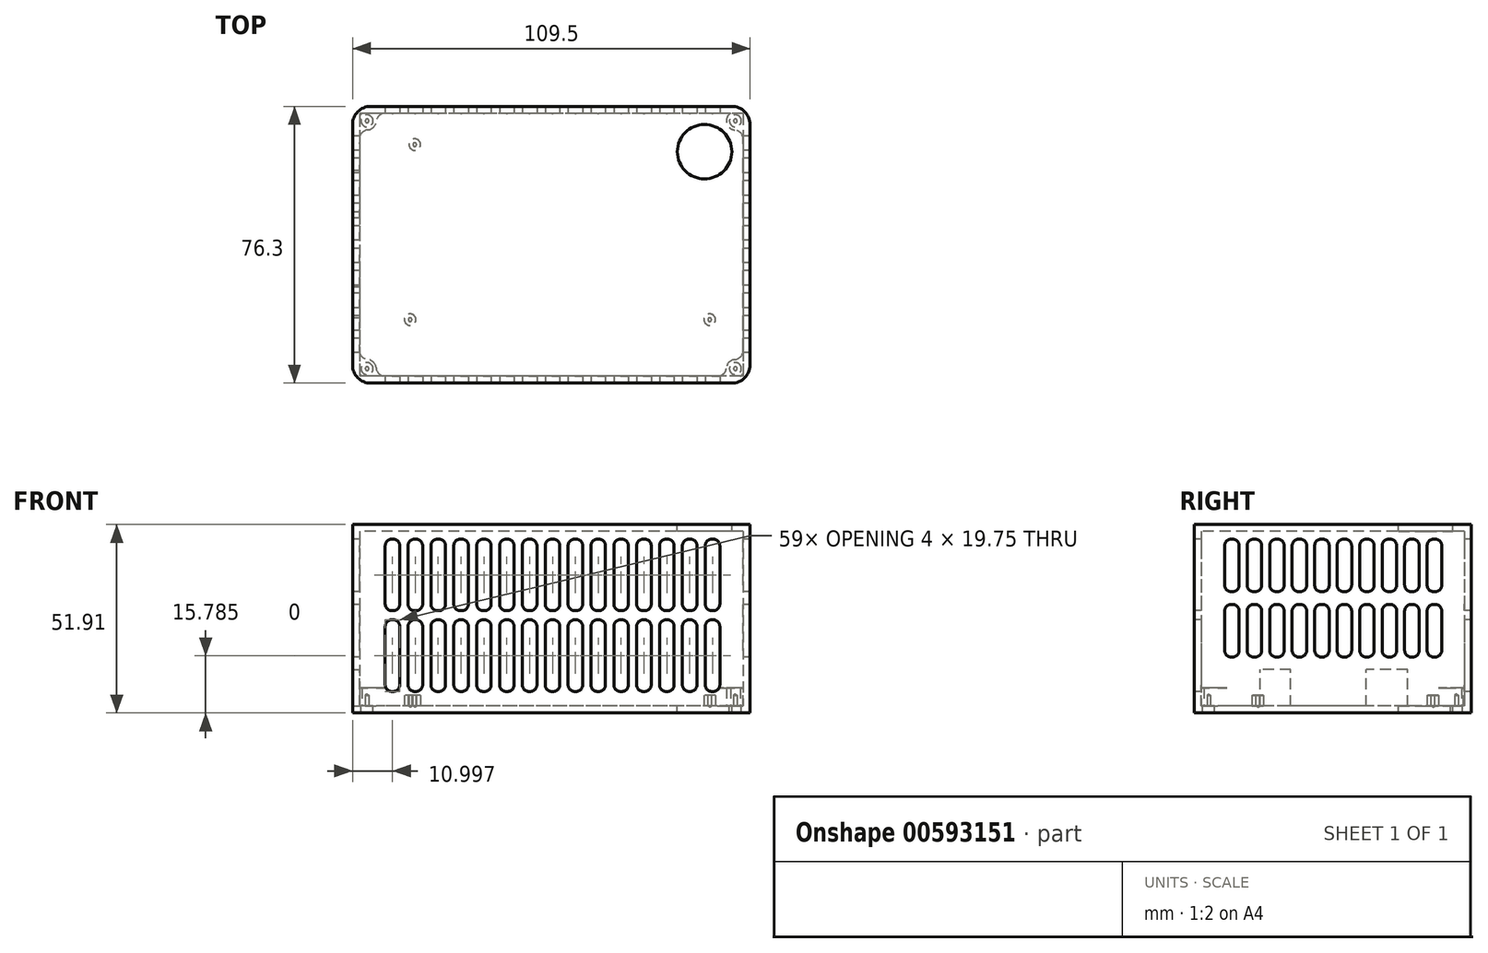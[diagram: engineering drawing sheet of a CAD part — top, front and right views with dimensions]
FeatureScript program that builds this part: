
annotation { "Feature Type Name" : "Feature", "Feature Type Description" : "" }
export const myFeature = defineFeature(function(context is Context, id is Id, definition is map)
    precondition{}
    {
        {
            var Q0;
            Q0=qCreatedBy(makeId("Top.planeOp"),FACE);
            var sketch = newSketch(context, id + "F0", { "sketchPlane" : qUnion([Q0])});
            skLineSegment(sketch, "E0.bottom", {"start": v(-36.54, 23.72) * mm, "end": v(59.98, 23.72) * mm});
            skLineSegment(sketch, "E0.top", {"start": v(-36.54, -29.62) * mm, "end": v(62.52, -29.62) * mm});
            skLineSegment(sketch, "E0.left", {"start": v(-36.54, 23.72) * mm, "end": v(-36.54, -29.62) * mm});
            skCircle(sketch, "E1", {"center": v(-21.3, 21.18) * mm, "radius": 1.59 * mm});
            skCircle(sketch, "E2", {"center": v(53.63, 21.18) * mm, "radius": 1.6 * mm});
            skCircle(sketch, "E3", {"center": v(-22.57, -27.08) * mm, "radius": 1.6 * mm});
            skCircle(sketch, "E4", {"center": v(59.98, -27.08) * mm, "radius": 1.6 * mm});
            skCircle(sketch, "E5", {"center": v(29.5, -22) * mm, "radius": 1.6 * mm});
            skCircle(sketch, "E6", {"center": v(29.5, 5.94) * mm, "radius": 1.6 * mm});
            skLineSegment(sketch, "E7.0", {"start": v(62.52, 21.18) * mm, "end": v(62.52, 11.02) * mm});
            skLineSegment(sketch, "E8.0", {"start": v(65.06, 8.48) * mm, "end": v(65.06, -25.81) * mm});
            skLineSegment(sketch, "E9", {"start": v(62.52, -28.35) * mm, "end": v(65.06, -25.81) * mm});
            skLineSegment(sketch, "E10", {"start": v(65.06, 8.48) * mm, "end": v(62.52, 11.02) * mm});
            skLineSegment(sketch, "E11", {"start": v(62.52, 21.18) * mm, "end": v(59.98, 23.72) * mm});
            skLineSegment(sketch, "E12", {"start": v(62.52, -28.35) * mm, "end": v(62.52, -29.62) * mm});
            skLineSegment(sketch, "E13.bottom", {"start": v(-42.89, 14.2) * mm, "end": v(-27.01, 14.2) * mm});
            skLineSegment(sketch, "E13.top", {"start": v(-42.89, 2.76) * mm, "end": v(-27.01, 2.76) * mm});
            skLineSegment(sketch, "E13.left", {"start": v(-42.89, 14.2) * mm, "end": v(-42.89, 2.76) * mm});
            skLineSegment(sketch, "E13.right", {"start": v(-27.01, 14.2) * mm, "end": v(-27.01, 2.76) * mm});
            skLineSegment(sketch, "E14.bottom", {"start": v(-38.44, -18.01) * mm, "end": v(-25.1, -18.01) * mm});
            skLineSegment(sketch, "E14.top", {"start": v(-38.44, -26.45) * mm, "end": v(-25.1, -26.45) * mm});
            skLineSegment(sketch, "E14.left", {"start": v(-38.44, -18.01) * mm, "end": v(-38.44, -26.45) * mm});
            skLineSegment(sketch, "E14.right", {"start": v(-25.1, -18.01) * mm, "end": v(-25.1, -26.45) * mm});
            skCircle(sketch, "E15", {"center": v(-17.74, 21.15) * mm, "radius": 0.51 * mm});
            skCircle(sketch, "E16.1.0.0", {"center": v(-15.2, 21.15) * mm, "radius": 0.51 * mm});
            skCircle(sketch, "E16.2.0.0", {"center": v(-12.66, 21.15) * mm, "radius": 0.51 * mm});
            skCircle(sketch, "E16.3.0.0", {"center": v(-10.12, 21.15) * mm, "radius": 0.51 * mm});
            skCircle(sketch, "E16.4.0.0", {"center": v(-7.58, 21.15) * mm, "radius": 0.51 * mm});
            skCircle(sketch, "E16.5.0.0", {"center": v(-5.04, 21.15) * mm, "radius": 0.51 * mm});
            skCircle(sketch, "E16.6.0.0", {"center": v(-2.5, 21.15) * mm, "radius": 0.51 * mm});
            skCircle(sketch, "E16.7.0.0", {"center": v(0.04, 21.15) * mm, "radius": 0.51 * mm});
            skCircle(sketch, "E16.8.0.0", {"center": v(2.58, 21.15) * mm, "radius": 0.51 * mm});
            skCircle(sketch, "E16.9.0.0", {"center": v(5.12, 21.15) * mm, "radius": 0.51 * mm});
            skLineSegment(sketch, "E16.direction1", {"start": v(-17.74, 21.15) * mm, "end": v(-15.2, 21.15) * mm, "construction": true});
            skCircle(sketch, "E17", {"center": v(9.18, 21.15) * mm, "radius": 0.5 * mm});
            skCircle(sketch, "E18.1.0.0", {"center": v(11.72, 21.15) * mm, "radius": 0.5 * mm});
            skCircle(sketch, "E18.2.0.0", {"center": v(14.26, 21.15) * mm, "radius": 0.5 * mm});
            skCircle(sketch, "E18.3.0.0", {"center": v(16.8, 21.15) * mm, "radius": 0.5 * mm});
            skCircle(sketch, "E18.4.0.0", {"center": v(19.34, 21.15) * mm, "radius": 0.5 * mm});
            skCircle(sketch, "E18.5.0.0", {"center": v(21.88, 21.15) * mm, "radius": 0.5 * mm});
            skCircle(sketch, "E18.6.0.0", {"center": v(24.42, 21.15) * mm, "radius": 0.5 * mm});
            skCircle(sketch, "E18.7.0.0", {"center": v(26.96, 21.15) * mm, "radius": 0.5 * mm});
            skLineSegment(sketch, "E18.direction1", {"start": v(9.18, 21.15) * mm, "end": v(11.72, 21.15) * mm, "construction": true});
            skCircle(sketch, "E19", {"center": v(32.04, 21.15) * mm, "radius": 0.5 * mm});
            skCircle(sketch, "E20.1.0.0", {"center": v(34.58, 21.15) * mm, "radius": 0.5 * mm});
            skCircle(sketch, "E20.2.0.0", {"center": v(37.12, 21.15) * mm, "radius": 0.5 * mm});
            skCircle(sketch, "E20.3.0.0", {"center": v(39.66, 21.15) * mm, "radius": 0.5 * mm});
            skCircle(sketch, "E20.4.0.0", {"center": v(42.2, 21.15) * mm, "radius": 0.5 * mm});
            skCircle(sketch, "E20.5.0.0", {"center": v(44.74, 21.15) * mm, "radius": 0.5 * mm});
            skCircle(sketch, "E20.6.0.0", {"center": v(47.28, 21.15) * mm, "radius": 0.5 * mm});
            skCircle(sketch, "E20.7.0.0", {"center": v(49.82, 21.15) * mm, "radius": 0.5 * mm});
            skLineSegment(sketch, "E20.direction1", {"start": v(32.04, 21.15) * mm, "end": v(34.58, 21.15) * mm, "construction": true});
            skCircle(sketch, "E21", {"center": v(-8.6, -27.08) * mm, "radius": 0.5 * mm});
            skCircle(sketch, "E22.1.0.0", {"center": v(-6.06, -27.08) * mm, "radius": 0.5 * mm});
            skCircle(sketch, "E22.2.0.0", {"center": v(-3.52, -27.08) * mm, "radius": 0.5 * mm});
            skCircle(sketch, "E22.3.0.0", {"center": v(-0.98, -27.08) * mm, "radius": 0.5 * mm});
            skCircle(sketch, "E22.4.0.0", {"center": v(1.56, -27.08) * mm, "radius": 0.5 * mm});
            skCircle(sketch, "E22.5.0.0", {"center": v(4.1, -27.08) * mm, "radius": 0.5 * mm});
            skCircle(sketch, "E22.6.0.0", {"center": v(6.64, -27.08) * mm, "radius": 0.5 * mm});
            skCircle(sketch, "E22.7.0.0", {"center": v(9.18, -27.08) * mm, "radius": 0.5 * mm});
            skLineSegment(sketch, "E22.direction1", {"start": v(-8.6, -27.08) * mm, "end": v(-6.06, -27.08) * mm, "construction": true});
            skCircle(sketch, "E23", {"center": v(14.66, -27.08) * mm, "radius": 0.51 * mm});
            skCircle(sketch, "E24.1.0.0", {"center": v(17.2, -27.08) * mm, "radius": 0.51 * mm});
            skCircle(sketch, "E24.2.0.0", {"center": v(19.74, -27.08) * mm, "radius": 0.51 * mm});
            skCircle(sketch, "E24.3.0.0", {"center": v(22.28, -27.08) * mm, "radius": 0.51 * mm});
            skCircle(sketch, "E24.4.0.0", {"center": v(24.82, -27.08) * mm, "radius": 0.51 * mm});
            skCircle(sketch, "E24.5.0.0", {"center": v(27.36, -27.08) * mm, "radius": 0.51 * mm});
            skCircle(sketch, "E24.6.0.0", {"center": v(29.9, -27.08) * mm, "radius": 0.51 * mm});
            skCircle(sketch, "E24.7.0.0", {"center": v(32.44, -27.08) * mm, "radius": 0.51 * mm});
            skLineSegment(sketch, "E24.direction1", {"start": v(14.66, -27.08) * mm, "end": v(17.2, -27.08) * mm, "construction": true});
            skCircle(sketch, "E25", {"center": v(37.12, -27.08) * mm, "radius": 0.5 * mm});
            skCircle(sketch, "E26.1.0.0", {"center": v(39.66, -27.08) * mm, "radius": 0.5 * mm});
            skCircle(sketch, "E26.2.0.0", {"center": v(42.2, -27.08) * mm, "radius": 0.5 * mm});
            skCircle(sketch, "E26.3.0.0", {"center": v(44.74, -27.08) * mm, "radius": 0.5 * mm});
            skCircle(sketch, "E26.4.0.0", {"center": v(47.28, -27.08) * mm, "radius": 0.5 * mm});
            skCircle(sketch, "E26.5.0.0", {"center": v(49.82, -27.08) * mm, "radius": 0.5 * mm});
            skCircle(sketch, "E26.6.0.0", {"center": v(52.36, -27.08) * mm, "radius": 0.5 * mm});
            skCircle(sketch, "E26.7.0.0", {"center": v(54.9, -27.08) * mm, "radius": 0.5 * mm});
            skLineSegment(sketch, "E26.direction1", {"start": v(37.12, -27.08) * mm, "end": v(39.66, -27.08) * mm, "construction": true});
            skCircle(sketch, "E27", {"center": v(59.98, 21.18) * mm, "radius": 0.5 * mm});
            skCircle(sketch, "E28.1.0.0", {"center": v(60, 18.64) * mm, "radius": 0.5 * mm});
            skCircle(sketch, "E28.2.0.0", {"center": v(60, 16.1) * mm, "radius": 0.5 * mm});
            skCircle(sketch, "E28.3.0.0", {"center": v(60, 13.56) * mm, "radius": 0.5 * mm});
            skCircle(sketch, "E28.4.0.0", {"center": v(60.02, 11.02) * mm, "radius": 0.5 * mm});
            skCircle(sketch, "E28.5.0.0", {"center": v(60.03, 8.48) * mm, "radius": 0.5 * mm});
            skCircle(sketch, "E28.6.0.0", {"center": v(60.04, 5.94) * mm, "radius": 0.5 * mm});
            skCircle(sketch, "E28.7.0.0", {"center": v(60.04, 3.4) * mm, "radius": 0.5 * mm});
            skCircle(sketch, "E28.8.0.0", {"center": v(60.05, 0.86) * mm, "radius": 0.5 * mm});
            skCircle(sketch, "E28.9.0.0", {"center": v(60.06, -1.68) * mm, "radius": 0.5 * mm});
            skCircle(sketch, "E28.10.0.0", {"center": v(60.07, -4.22) * mm, "radius": 0.5 * mm});
            skCircle(sketch, "E28.11.0.0", {"center": v(60.08, -6.76) * mm, "radius": 0.5 * mm});
            skCircle(sketch, "E28.12.0.0", {"center": v(60.09, -9.3) * mm, "radius": 0.5 * mm});
            skCircle(sketch, "E28.13.0.0", {"center": v(60.1, -11.84) * mm, "radius": 0.5 * mm});
            skCircle(sketch, "E28.14.0.0", {"center": v(60.1, -14.38) * mm, "radius": 0.5 * mm});
            skCircle(sketch, "E28.15.0.0", {"center": v(60.12, -16.92) * mm, "radius": 0.5 * mm});
            skCircle(sketch, "E28.16.0.0", {"center": v(60.13, -19.46) * mm, "radius": 0.5 * mm});
            skCircle(sketch, "E28.17.0.0", {"center": v(60.14, -22) * mm, "radius": 0.5 * mm});
            skLineSegment(sketch, "E28.direction1", {"start": v(59.98, 21.18) * mm, "end": v(60, 18.64) * mm, "construction": true});
            skCircle(sketch, "E29", {"center": v(57.44, 21.15) * mm, "radius": 0.5 * mm});
            skCircle(sketch, "E30.1.0.0", {"center": v(57.44, 18.61) * mm, "radius": 0.5 * mm});
            skCircle(sketch, "E30.2.0.0", {"center": v(57.43, 16.07) * mm, "radius": 0.5 * mm});
            skCircle(sketch, "E30.3.0.0", {"center": v(57.42, 13.53) * mm, "radius": 0.5 * mm});
            skCircle(sketch, "E30.4.0.0", {"center": v(57.42, 11) * mm, "radius": 0.5 * mm});
            skCircle(sketch, "E30.5.0.0", {"center": v(57.4, 8.45) * mm, "radius": 0.5 * mm});
            skCircle(sketch, "E30.6.0.0", {"center": v(57.4, 5.91) * mm, "radius": 0.5 * mm});
            skCircle(sketch, "E30.7.0.0", {"center": v(57.4, 3.37) * mm, "radius": 0.5 * mm});
            skCircle(sketch, "E30.8.0.0", {"center": v(57.39, 0.83) * mm, "radius": 0.5 * mm});
            skCircle(sketch, "E30.9.0.0", {"center": v(57.38, -1.7) * mm, "radius": 0.5 * mm});
            skCircle(sketch, "E30.10.0.0", {"center": v(57.38, -4.25) * mm, "radius": 0.5 * mm});
            skCircle(sketch, "E30.11.0.0", {"center": v(57.37, -6.79) * mm, "radius": 0.5 * mm});
            skCircle(sketch, "E30.12.0.0", {"center": v(57.36, -9.33) * mm, "radius": 0.5 * mm});
            skCircle(sketch, "E30.13.0.0", {"center": v(57.36, -11.87) * mm, "radius": 0.5 * mm});
            skCircle(sketch, "E30.14.0.0", {"center": v(57.35, -14.4) * mm, "radius": 0.5 * mm});
            skCircle(sketch, "E30.15.0.0", {"center": v(57.34, -16.95) * mm, "radius": 0.5 * mm});
            skCircle(sketch, "E30.16.0.0", {"center": v(57.34, -19.49) * mm, "radius": 0.5 * mm});
            skCircle(sketch, "E30.17.0.0", {"center": v(57.33, -22.03) * mm, "radius": 0.5 * mm});
            skLineSegment(sketch, "E30.direction1", {"start": v(57.44, 21.15) * mm, "end": v(57.44, 18.61) * mm, "construction": true});
            skCircle(sketch, "E31", {"center": v(27.09, 0.86) * mm, "radius": 0.5 * mm});
            skCircle(sketch, "E32", {"center": v(29.63, 0.86) * mm, "radius": 0.5 * mm});
            skCircle(sketch, "E33.1.0.0", {"center": v(27.1, -1.68) * mm, "radius": 0.5 * mm});
            skCircle(sketch, "E33.2.0.0", {"center": v(27.1, -4.22) * mm, "radius": 0.5 * mm});
            skLineSegment(sketch, "E33.direction1", {"start": v(27.09, 0.86) * mm, "end": v(27.1, -1.68) * mm, "construction": true});
            skCircle(sketch, "E34.1.0.0", {"center": v(29.62, -1.68) * mm, "radius": 0.5 * mm});
            skCircle(sketch, "E34.2.0.0", {"center": v(29.62, -4.22) * mm, "radius": 0.5 * mm});
            skLineSegment(sketch, "E34.direction1", {"start": v(29.63, 0.86) * mm, "end": v(29.62, -1.68) * mm, "construction": true});
            skSolve(sketch);
        }
        {
            var Q0;
            Q0=qCreatedBy(makeId("Top.planeOp"),FACE);
            var sketch = newSketch(context, id + "F1", { "sketchPlane" : qUnion([Q0])});
            skLineSegment(sketch, "E35.bottom", {"start": v(-36.54, 23.72) * mm, "end": v(65.06, 23.72) * mm});
            skLineSegment(sketch, "E35.top", {"start": v(-36.54, -36.58) * mm, "end": v(65.06, -36.58) * mm});
            skLineSegment(sketch, "E35.left", {"start": v(-36.54, 23.72) * mm, "end": v(-36.54, -36.58) * mm});
            skLineSegment(sketch, "E35.right", {"start": v(65.06, 23.72) * mm, "end": v(65.06, -36.58) * mm});
            skCircle(sketch, "E36", {"center": v(-21.3, 21.18) * mm, "radius": 1.9 * mm});
            skCircle(sketch, "E37", {"center": v(-22.54, -27.08) * mm, "radius": 1.9 * mm});
            skCircle(sketch, "E38", {"center": v(59.96, -27.08) * mm, "radius": 1.9 * mm});
            skLineSegment(sketch, "E39.0", {"start": v(-36.54, 23.72) * mm, "end": v(59.98, 23.72) * mm});
            skLineSegment(sketch, "E40.0", {"start": v(65.06, 8.48) * mm, "end": v(65.06, -25.81) * mm});
            skLineSegment(sketch, "E41.bottom", {"start": v(-39.16, -12.96) * mm, "end": v(-27.16, -12.96) * mm});
            skLineSegment(sketch, "E41.top", {"start": v(-39.16, -35.2) * mm, "end": v(-27.16, -35.2) * mm});
            skLineSegment(sketch, "E41.left", {"start": v(-39.16, -12.96) * mm, "end": v(-39.16, -35.2) * mm});
            skLineSegment(sketch, "E41.right", {"start": v(-27.16, -12.96) * mm, "end": v(-27.16, -35.2) * mm});
            skSolve(sketch);
        }
        {
            var Q0;
            Q0=qCreatedBy(makeId("Top.planeOp"),FACE);
            var sketch = newSketch(context, id + "F2", { "sketchPlane" : qUnion([Q0])});
            skLineSegment(sketch, "E42.bottom", {"start": v(71.06, 31.72) * mm, "end": v(-38.44, 31.72) * mm});
            skLineSegment(sketch, "E42.top", {"start": v(71.06, -44.58) * mm, "end": v(-38.44, -44.58) * mm});
            skLineSegment(sketch, "E42.left", {"start": v(71.06, 31.72) * mm, "end": v(71.06, -44.58) * mm});
            skLineSegment(sketch, "E43.0", {"start": v(-42.89, 14.2) * mm, "end": v(-42.89, 2.76) * mm});
            skLineSegment(sketch, "E44.0", {"start": v(-38.44, 31.72) * mm, "end": v(-38.44, -44.58) * mm});
            skSolve(sketch);
        }
        {
            var Q0;
            {var subQ1=sQuery(id+"F2.wireOp",EDGE,"E42.bottom");Q0=makeQuery(id+"F2.imprint","IMPRINT",FACE,{"disambiguationData":[TD([[makeQuery(id+"F2.imprint","IMPRINT",EDGE,{"derivedFrom":subQ1}),1.0]])]});}
            extrude(context, id + "F3", {"entities" : qUnion([Q0]), "depth" : 50 * mm, "offsetDistance" : 25 * mm});
        }
        {
            var Q0;
            Q0=makeQuery(id+"F3.opExtrude","CAP_FACE",FACE,{"disambiguationData":[OSD([sQuery(id+"F2.wireOp",EDGE,"E42.bottom"),sQuery(id+"F2.wireOp",EDGE,"E42.top"),sQuery(id+"F2.wireOp",EDGE,"E42.left"),sQuery(id+"F2.wireOp",EDGE,"E42.right"),sQuery(id+"F2.wireOp",EDGE,"E43.0")])],"isStart":true});
            shell(context, id + "F4", {"entities" : qUnion([Q0]), "thickness" : 1.9 * mm});
        }
        {
            var Q0;
            Q0=makeQuery(id+"F2.imprint","IMPRINT",FACE,{"disambiguationData":[TD([[makeQuery(id+"F2.imprint","IMPRINT",EDGE,{"derivedFrom":sQuery(id+"F2.wireOp",EDGE,"E42.bottom")}),1.0]])]});
            extrude(context, id + "F5", {"entities" : qUnion([Q0]), "oppositeDirection" : true, "depth" : 1.9 * mm, "offsetDistance" : 25 * mm});
        }
        {
            var Q0;
            {var subQ5=sQuery(id+"F0.wireOp",EDGE,"E13.right");Q0=makeQuery(id+"F0.imprint","IMPRINT",FACE,{"disambiguationData":[TD([[makeQuery(id+"F0.imprint","IMPRINT",EDGE,{"derivedFrom":subQ5}),-1.0]])]});}
            var Q1;
            {var subQ5=sQuery(id+"F0.wireOp",EDGE,"E13.left");Q1=makeQuery(id+"F0.imprint","IMPRINT",FACE,{"disambiguationData":[TD([[makeQuery(id+"F0.imprint","IMPRINT",EDGE,{"derivedFrom":subQ5}),1.0]])]});}
            extrude(context, id + "F6", {"entities" : qUnion([Q0, Q1]), "operationType" : NewBodyOperationType.REMOVE, "depth" : 10 * mm, "offsetDistance" : 25 * mm});
        }
        {
            var Q0;
            {var subQ5=sQuery(id+"F0.wireOp",EDGE,"E14.right");Q0=makeQuery(id+"F0.imprint","IMPRINT",FACE,{"disambiguationData":[TD([[makeQuery(id+"F0.imprint","IMPRINT",EDGE,{"derivedFrom":subQ5}),-1.0]])]});}
            var Q1;
            {var subQ5=sQuery(id+"F0.wireOp",EDGE,"E14.left");Q1=makeQuery(id+"F0.imprint","IMPRINT",FACE,{"disambiguationData":[TD([[makeQuery(id+"F0.imprint","IMPRINT",EDGE,{"derivedFrom":subQ5}),1.0]])]});}
            extrude(context, id + "F7", {"entities" : qUnion([Q0, Q1]), "operationType" : NewBodyOperationType.REMOVE, "depth" : 10 * mm, "offsetDistance" : 25 * mm});
        }
        {
            var Q0;
            Q0=makeQuery(id+"F0.imprint","IMPRINT",FACE,{"disambiguationData":[TD([[makeQuery(id+"F0.imprint","IMPRINT",EDGE,{"derivedFrom":sQuery(id+"F0.wireOp",EDGE,"E1")}),1.0]])]});
            var Q1;
            Q1=makeQuery(id+"F0.imprint","IMPRINT",FACE,{"disambiguationData":[TD([[makeQuery(id+"F0.imprint","IMPRINT",EDGE,{"derivedFrom":sQuery(id+"F0.wireOp",EDGE,"E3")}),1.0]])]});
            var Q2;
            Q2=makeQuery(id+"F0.imprint","IMPRINT",FACE,{"disambiguationData":[TD([[makeQuery(id+"F0.imprint","IMPRINT",EDGE,{"derivedFrom":sQuery(id+"F0.wireOp",EDGE,"E2")}),1.0]])]});
            var Q3;
            Q3=makeQuery(id+"F0.imprint","IMPRINT",FACE,{"disambiguationData":[TD([[makeQuery(id+"F0.imprint","IMPRINT",EDGE,{"derivedFrom":sQuery(id+"F0.wireOp",EDGE,"E4")}),1.0]])]});
            extrude(context, id + "F8", {"entities" : qUnion([Q0, Q1, Q2, Q3]), "operationType" : NewBodyOperationType.ADD, "depth" : 3 * mm, "offsetDistance" : 25 * mm});
        }
        {
            var Q0;
            Q0=makeQuery(id+"F2.imprint","IMPRINT",FACE,{"disambiguationData":[TD([[makeQuery(id+"F2.imprint","IMPRINT",EDGE,{"derivedFrom":sQuery(id+"F2.wireOp",EDGE,"E42.bottom")}),1.0]])]});
            var sketch = newSketch(context, id + "F9", { "sketchPlane" : qUnion([Q0])});
            skLineSegment(sketch, "E45.0", {"start": v(67.06, 27.72) * mm, "end": v(-34.44, 27.72) * mm});
            skLineSegment(sketch, "E45.1", {"start": v(67.06, 27.72) * mm, "end": v(67.06, -40.58) * mm});
            skLineSegment(sketch, "E45.2", {"start": v(67.06, -40.58) * mm, "end": v(-34.44, -40.58) * mm});
            skLineSegment(sketch, "E45.3", {"start": v(-34.44, 27.72) * mm, "end": v(-34.44, -40.58) * mm});
            skCircle(sketch, "E46", {"center": v(67.06, 27.72) * mm, "radius": 2.5 * mm});
            skCircle(sketch, "E47", {"center": v(67.06, -40.58) * mm, "radius": 2.5 * mm});
            skCircle(sketch, "E48", {"center": v(-34.44, 27.72) * mm, "radius": 2.5 * mm});
            skCircle(sketch, "E49", {"center": v(-34.44, -40.58) * mm, "radius": 2.5 * mm});
            skSolve(sketch);
        }
        {
            var Q0;
            Q0=sQuery(id+"F9.wireOp",VERTEX,"E45.0.end");
            var Q1;
            Q1=sQuery(id+"F9.wireOp",VERTEX,"E45.1.start");
            var Q2;
            Q2=sQuery(id+"F9.wireOp",VERTEX,"E45.1.end");
            var Q3;
            Q3=sQuery(id+"F9.wireOp",VERTEX,"E45.3.end");
            var Q4;
            Q4=makeQuery(id+"F5.opExtrude","SWEPT_BODY",BODY,{"disambiguationData":[OSD([sQuery(id+"F2.wireOp",EDGE,"E42.bottom"),sQuery(id+"F2.wireOp",EDGE,"E42.top"),sQuery(id+"F2.wireOp",EDGE,"E42.left"),sQuery(id+"F2.wireOp",EDGE,"E44.0")])]});
            hole(context, id + "F10", {"style" : HoleStyle.SIMPLE, "endStyle" : HoleEndStyle.THROUGH, "standardTappedOrClearance" : lookupTablePath({ "standard" : "ISO", "fit" : "Normal", "size" : "M3", "type" : "Clearance" }), "standardBlindInLast" : lookupTablePath({ "fit" : "Standard", "standard" : "ISO", "size" : "M3", "type" : "Clearance" }), "holeDiameter" : 3.3 * mm, "majorDiameter" : 5 * mm, "isTappedThrough" : true, "tappedDepth" : 12 * mm, "tapClearance" : 3, "locations" : qUnion([Q0, Q1, Q2, Q3]), "scope" : qUnion([Q4])});
        }
        {
            var Q0;
            Q0=makeQuery(id+"F8.opExtrude","CAP_FACE",FACE,{"disambiguationData":[OSD([sQuery(id+"F0.wireOp",EDGE,"E1")])],"isStart":false});
            var sketch = newSketch(context, id + "F11", { "sketchPlane" : qUnion([Q0])});
            skCircle(sketch, "E50.0", {"center": v(-22.57, -27.08) * mm, "radius": 1.6 * mm});
            skCircle(sketch, "E51.0", {"center": v(-21.3, 21.18) * mm, "radius": 1.59 * mm});
            skCircle(sketch, "E52.0", {"center": v(59.98, -27.08) * mm, "radius": 1.6 * mm});
            skCircle(sketch, "E53.0", {"center": v(53.63, 21.18) * mm, "radius": 1.6 * mm});
            skSolve(sketch);
        }
        {
            var Q0;
            Q0=sQuery(id+"F11.wireOp",VERTEX,"E50.0.center");
            var Q1;
            Q1=sQuery(id+"F11.wireOp",VERTEX,"E51.0.center");
            var Q2;
            Q2=sQuery(id+"F11.wireOp",VERTEX,"E52.0.center");
            var Q3;
            Q3=sQuery(id+"F11.wireOp",VERTEX,"E53.0.center");
            var Q4;
            Q4=makeQuery(id+"F5.opExtrude","SWEPT_BODY",BODY,{"disambiguationData":[OSD([sQuery(id+"F2.wireOp",EDGE,"E42.bottom"),sQuery(id+"F2.wireOp",EDGE,"E42.top"),sQuery(id+"F2.wireOp",EDGE,"E42.left"),sQuery(id+"F2.wireOp",EDGE,"E44.0")])]});
            hole(context, id + "F12", {"style" : HoleStyle.SIMPLE, "endStyle" : HoleEndStyle.BLIND, "standardTappedOrClearance" : lookupTablePath({ "standard" : "ISO", "size" : "1", "type" : "Drilled" }), "standardBlindInLast" : lookupTablePath({ "standard" : "ISO", "size" : "1", "type" : "Drilled" }), "holeDiameter" : 1 * mm, "majorDiameter" : 5 * mm, "holeDepth" : 3 * mm, "isTappedThrough" : true, "tappedDepth" : 12 * mm, "tapClearance" : 3, "locations" : qUnion([Q0, Q1, Q2, Q3]), "scope" : qUnion([Q4])});
        }
        {
            var Q0;
            {var subQ0=sQuery(id+"F9.wireOp",EDGE,"E45.1");var subQ1=sQuery(id+"F9.wireOp",EDGE,"E45.0");var subQ2=makeQuery(id+"F9.imprint","INTERSECT",VERTEX,{"derivedFrom":[subQ1,subQ0]});Q0=makeQuery(id+"F9.imprint","IMPRINT",FACE,{"disambiguationData":[TD([[makeQuery(id+"F9.imprint","IMPRINT",EDGE,{"disambiguationData":[TD([[subQ2,-1.0]])],"derivedFrom":subQ1}),-1.0]])]});}
            var Q1;
            {var subQ0=sQuery(id+"F9.wireOp",EDGE,"E45.1");var subQ1=sQuery(id+"F9.wireOp",EDGE,"E45.0");var subQ2=makeQuery(id+"F9.imprint","INTERSECT",VERTEX,{"derivedFrom":[subQ1,subQ0]});Q1=makeQuery(id+"F9.imprint","IMPRINT",FACE,{"disambiguationData":[TD([[makeQuery(id+"F9.imprint","IMPRINT",EDGE,{"disambiguationData":[TD([[subQ2,-1.0]])],"derivedFrom":subQ1}),1.0]])]});}
            var Q2;
            {var subQ0=sQuery(id+"F9.wireOp",EDGE,"E45.2");var subQ1=sQuery(id+"F9.wireOp",EDGE,"E45.1");var subQ2=makeQuery(id+"F9.imprint","INTERSECT",VERTEX,{"derivedFrom":[subQ1,subQ0]});Q2=makeQuery(id+"F9.imprint","IMPRINT",FACE,{"disambiguationData":[TD([[makeQuery(id+"F9.imprint","IMPRINT",EDGE,{"disambiguationData":[TD([[subQ2,1.0]])],"derivedFrom":subQ1}),-1.0]])]});}
            var Q3;
            {var subQ0=sQuery(id+"F9.wireOp",EDGE,"E45.2");var subQ1=sQuery(id+"F9.wireOp",EDGE,"E45.1");var subQ2=makeQuery(id+"F9.imprint","INTERSECT",VERTEX,{"derivedFrom":[subQ1,subQ0]});Q3=makeQuery(id+"F9.imprint","IMPRINT",FACE,{"disambiguationData":[TD([[makeQuery(id+"F9.imprint","IMPRINT",EDGE,{"disambiguationData":[TD([[subQ2,1.0]])],"derivedFrom":subQ1}),1.0]])]});}
            var Q4;
            {var subQ0=sQuery(id+"F9.wireOp",EDGE,"E45.3");var subQ1=sQuery(id+"F9.wireOp",EDGE,"E45.0");var subQ2=makeQuery(id+"F9.imprint","INTERSECT",VERTEX,{"derivedFrom":[subQ1,subQ0]});Q4=makeQuery(id+"F9.imprint","IMPRINT",FACE,{"disambiguationData":[TD([[makeQuery(id+"F9.imprint","IMPRINT",EDGE,{"disambiguationData":[TD([[subQ2,1.0]])],"derivedFrom":subQ1}),-1.0]])]});}
            var Q5;
            {var subQ0=sQuery(id+"F9.wireOp",EDGE,"E45.3");var subQ1=sQuery(id+"F9.wireOp",EDGE,"E45.0");var subQ2=makeQuery(id+"F9.imprint","INTERSECT",VERTEX,{"derivedFrom":[subQ1,subQ0]});Q5=makeQuery(id+"F9.imprint","IMPRINT",FACE,{"disambiguationData":[TD([[makeQuery(id+"F9.imprint","IMPRINT",EDGE,{"disambiguationData":[TD([[subQ2,1.0]])],"derivedFrom":subQ1}),1.0]])]});}
            var Q6;
            {var subQ0=sQuery(id+"F9.wireOp",EDGE,"E45.3");var subQ1=sQuery(id+"F9.wireOp",EDGE,"E45.2");var subQ2=makeQuery(id+"F9.imprint","INTERSECT",VERTEX,{"derivedFrom":[subQ1,subQ0]});Q6=makeQuery(id+"F9.imprint","IMPRINT",FACE,{"disambiguationData":[TD([[makeQuery(id+"F9.imprint","IMPRINT",EDGE,{"disambiguationData":[TD([[subQ2,1.0]])],"derivedFrom":subQ1}),-1.0]])]});}
            var Q7;
            {var subQ0=sQuery(id+"F9.wireOp",EDGE,"E45.3");var subQ1=sQuery(id+"F9.wireOp",EDGE,"E45.2");var subQ2=makeQuery(id+"F9.imprint","INTERSECT",VERTEX,{"derivedFrom":[subQ1,subQ0]});Q7=makeQuery(id+"F9.imprint","IMPRINT",FACE,{"disambiguationData":[TD([[makeQuery(id+"F9.imprint","IMPRINT",EDGE,{"disambiguationData":[TD([[subQ2,1.0]])],"derivedFrom":subQ1}),1.0]])]});}
            extrude(context, id + "F13", {"entities" : qUnion([Q0, Q1, Q2, Q3, Q4, Q5, Q6, Q7]), "operationType" : NewBodyOperationType.ADD, "depth" : 5 * mm, "offsetDistance" : 25 * mm});
        }
        {
            var Q0;
            Q0=sQuery(id+"F9.wireOp",VERTEX,"E49.center");
            var Q1;
            Q1=sQuery(id+"F9.wireOp",VERTEX,"E45.1.end");
            var Q2;
            Q2=sQuery(id+"F9.wireOp",VERTEX,"E45.0.end");
            var Q3;
            Q3=sQuery(id+"F9.wireOp",VERTEX,"E45.1.start");
            var Q4;
            Q4=makeQuery(id+"F3.opExtrude","SWEPT_BODY",BODY,{"disambiguationData":[OSD([sQuery(id+"F2.wireOp",EDGE,"E42.bottom"),sQuery(id+"F2.wireOp",EDGE,"E42.top"),sQuery(id+"F2.wireOp",EDGE,"E42.left"),sQuery(id+"F2.wireOp",EDGE,"E44.0")])]});
            hole(context, id + "F14", {"style" : HoleStyle.SIMPLE, "endStyle" : HoleEndStyle.BLIND, "oppositeDirection" : true, "standardTappedOrClearance" : lookupTablePath({ "standard" : "ISO", "size" : "1", "type" : "Drilled" }), "standardBlindInLast" : lookupTablePath({ "standard" : "ISO", "size" : "1", "type" : "Drilled" }), "holeDiameter" : 1 * mm, "majorDiameter" : 5 * mm, "holeDepth" : 3 * mm, "isTappedThrough" : true, "tappedDepth" : 12 * mm, "tapClearance" : 3, "locations" : qUnion([Q0, Q1, Q2, Q3]), "scope" : qUnion([Q4])});
        }
        {
            var Q0;
            Q0=makeQuery(id+"F13.boolean.opBoolean","INTERSECT",EDGE,{"disambiguationData":[OD(1.0)],"derivedFrom":[makeQuery(id+"F4.opShell","OFFSET_FACE",FACE,{"disambiguationData":[OSD([sQuery(id+"F2.wireOp",EDGE,"E42.left")])]}),makeQuery(id+"F13.opExtrude","SWEPT_FACE",FACE,{"disambiguationData":[OSD([sQuery(id+"F9.wireOp",EDGE,"E47")])]})]});
            var Q1;
            Q1=makeQuery(id+"F13.boolean.opBoolean","INTERSECT",EDGE,{"disambiguationData":[OD(1.0)],"derivedFrom":[makeQuery(id+"F4.opShell","OFFSET_FACE",FACE,{"disambiguationData":[OSD([sQuery(id+"F2.wireOp",EDGE,"E42.top")])]}),makeQuery(id+"F13.opExtrude","SWEPT_FACE",FACE,{"disambiguationData":[OSD([sQuery(id+"F9.wireOp",EDGE,"E47")])]})]});
            var Q2;
            Q2=makeQuery(id+"F13.boolean.opBoolean","INTERSECT",EDGE,{"disambiguationData":[OD(1.0)],"derivedFrom":[makeQuery(id+"F4.opShell","OFFSET_FACE",FACE,{"disambiguationData":[OSD([sQuery(id+"F2.wireOp",EDGE,"E42.left")])]}),makeQuery(id+"F13.opExtrude","SWEPT_FACE",FACE,{"disambiguationData":[OSD([sQuery(id+"F9.wireOp",EDGE,"E46")])]})]});
            var Q3;
            Q3=makeQuery(id+"F13.boolean.opBoolean","INTERSECT",EDGE,{"disambiguationData":[OD(1.0)],"derivedFrom":[makeQuery(id+"F4.opShell","OFFSET_FACE",FACE,{"disambiguationData":[OSD([sQuery(id+"F2.wireOp",EDGE,"E42.bottom")])]}),makeQuery(id+"F13.opExtrude","SWEPT_FACE",FACE,{"disambiguationData":[OSD([sQuery(id+"F9.wireOp",EDGE,"E46")])]})]});
            var Q4;
            Q4=makeQuery(id+"F13.boolean.opBoolean","INTERSECT",EDGE,{"disambiguationData":[OD(1.0)],"derivedFrom":[makeQuery(id+"F4.opShell","OFFSET_FACE",FACE,{"disambiguationData":[OSD([sQuery(id+"F2.wireOp",EDGE,"E42.top")])]}),makeQuery(id+"F13.opExtrude","SWEPT_FACE",FACE,{"disambiguationData":[OSD([sQuery(id+"F9.wireOp",EDGE,"E49")])]})]});
            var Q5;
            Q5=makeQuery(id+"F13.boolean.opBoolean","INTERSECT",EDGE,{"disambiguationData":[OD(1.0)],"derivedFrom":[makeQuery(id+"F4.opShell","OFFSET_FACE",FACE,{"disambiguationData":[OSD([sQuery(id+"F2.wireOp",EDGE,"E44.0")])]}),makeQuery(id+"F13.opExtrude","SWEPT_FACE",FACE,{"disambiguationData":[OSD([sQuery(id+"F9.wireOp",EDGE,"E49")])]})]});
            var Q6;
            Q6=makeQuery(id+"F13.boolean.opBoolean","INTERSECT",EDGE,{"disambiguationData":[OD(1.0)],"derivedFrom":[makeQuery(id+"F4.opShell","OFFSET_FACE",FACE,{"disambiguationData":[OSD([sQuery(id+"F2.wireOp",EDGE,"E44.0")])]}),makeQuery(id+"F13.opExtrude","SWEPT_FACE",FACE,{"disambiguationData":[OSD([sQuery(id+"F9.wireOp",EDGE,"E48")])]})]});
            var Q7;
            Q7=makeQuery(id+"F13.boolean.opBoolean","INTERSECT",EDGE,{"disambiguationData":[OD(1.0)],"derivedFrom":[makeQuery(id+"F4.opShell","OFFSET_FACE",FACE,{"disambiguationData":[OSD([sQuery(id+"F2.wireOp",EDGE,"E42.bottom")])]}),makeQuery(id+"F13.opExtrude","SWEPT_FACE",FACE,{"disambiguationData":[OSD([sQuery(id+"F9.wireOp",EDGE,"E48")])]})]});
            fillet(context, id + "F15", {"entities" : qUnion([Q0, Q1, Q2, Q3, Q4, Q5, Q6, Q7]), "radius" : 2.5 * mm, "tangentPropagation" : true, "allowEdgeOverflow" : false});
        }
        {
            var Q0;
            Q0=makeQuery(id+"F3.opExtrude","SWEPT_EDGE",EDGE,{"disambiguationData":[OSD([sQuery(id+"F2.wireOp",EDGE,"E42.top"),sQuery(id+"F2.wireOp",EDGE,"E44.0")])]});
            var Q1;
            Q1=makeQuery(id+"F3.opExtrude","SWEPT_EDGE",EDGE,{"disambiguationData":[OSD([sQuery(id+"F2.wireOp",EDGE,"E42.top"),sQuery(id+"F2.wireOp",EDGE,"E42.left")])]});
            var Q2;
            Q2=makeQuery(id+"F3.opExtrude","SWEPT_EDGE",EDGE,{"disambiguationData":[OSD([sQuery(id+"F2.wireOp",EDGE,"E42.bottom"),sQuery(id+"F2.wireOp",EDGE,"E44.0")])]});
            var Q3;
            Q3=makeQuery(id+"F3.opExtrude","SWEPT_EDGE",EDGE,{"disambiguationData":[OSD([sQuery(id+"F2.wireOp",EDGE,"E42.bottom"),sQuery(id+"F2.wireOp",EDGE,"E42.left")])]});
            var Q4;
            Q4=makeQuery(id+"F5.opExtrude","SWEPT_EDGE",EDGE,{"disambiguationData":[OSD([sQuery(id+"F2.wireOp",EDGE,"E42.bottom"),sQuery(id+"F2.wireOp",EDGE,"E44.0")])]});
            var Q5;
            Q5=makeQuery(id+"F5.opExtrude","SWEPT_EDGE",EDGE,{"disambiguationData":[OSD([sQuery(id+"F2.wireOp",EDGE,"E42.top"),sQuery(id+"F2.wireOp",EDGE,"E44.0")])]});
            var Q6;
            Q6=makeQuery(id+"F5.opExtrude","SWEPT_EDGE",EDGE,{"disambiguationData":[OSD([sQuery(id+"F2.wireOp",EDGE,"E42.top"),sQuery(id+"F2.wireOp",EDGE,"E42.left")])]});
            var Q7;
            Q7=makeQuery(id+"F5.opExtrude","SWEPT_EDGE",EDGE,{"disambiguationData":[OSD([sQuery(id+"F2.wireOp",EDGE,"E42.bottom"),sQuery(id+"F2.wireOp",EDGE,"E42.left")])]});
            fillet(context, id + "F16", {"entities" : qUnion([Q0, Q1, Q2, Q3, Q4, Q5, Q6, Q7]), "radius" : 5 * mm, "tangentPropagation" : true, "allowEdgeOverflow" : false});
        }
        {
            var Q0;
            Q0=makeQuery(id+"F3.opExtrude","SWEPT_FACE",FACE,{"disambiguationData":[OSD([sQuery(id+"F2.wireOp",EDGE,"E42.top")])]});
            var sketch = newSketch(context, id + "F17", { "sketchPlane" : qUnion([Q0])});
            skLineSegment(sketch, "E54.bottom", {"start": v(-27.64, 46) * mm, "end": v(-27.24, 46) * mm});
            skLineSegment(sketch, "E54.top", {"start": v(-27.64, 26.25) * mm, "end": v(-27.24, 26.25) * mm});
            skLineSegment(sketch, "E54.left", {"start": v(-29.44, 44.2) * mm, "end": v(-29.44, 28.05) * mm});
            skLineSegment(sketch, "E54.right", {"start": v(-25.44, 44.2) * mm, "end": v(-25.44, 28.05) * mm});
            skPoint(sketch, "E55.visualSharp", {"position": v(-29.44, 46) * mm});
            skArc(sketch, "E55.filletArc", {"start": v(-27.64, 46) * mm, "mid": v(-28.92, 45.47) * mm, "end": v(-29.44, 44.2) * mm});
            skPoint(sketch, "E56.visualSharp", {"position": v(-25.44, 46) * mm});
            skArc(sketch, "E56.filletArc", {"start": v(-25.44, 44.2) * mm, "mid": v(-25.97, 45.47) * mm, "end": v(-27.24, 46) * mm});
            skArc(sketch, "E57.filletArc", {"start": v(-29.44, 28.05) * mm, "mid": v(-28.92, 26.78) * mm, "end": v(-27.64, 26.25) * mm});
            skArc(sketch, "E58.filletArc", {"start": v(-27.24, 26.25) * mm, "mid": v(-25.97, 26.78) * mm, "end": v(-25.44, 28.05) * mm});
            skLineSegment(sketch, "E59.0.1.0", {"start": v(-27.64, 23.75) * mm, "end": v(-27.24, 23.75) * mm});
            skArc(sketch, "E59.0.1.1", {"start": v(-25.44, 21.95) * mm, "mid": v(-25.97, 23.22) * mm, "end": v(-27.24, 23.75) * mm});
            skLineSegment(sketch, "E59.0.1.2", {"start": v(-25.44, 21.95) * mm, "end": v(-25.44, 5.8) * mm});
            skArc(sketch, "E59.0.1.3", {"start": v(-27.64, 23.75) * mm, "mid": v(-28.92, 23.22) * mm, "end": v(-29.44, 21.95) * mm});
            skLineSegment(sketch, "E59.0.1.4", {"start": v(-29.44, 21.95) * mm, "end": v(-29.44, 5.8) * mm});
            skArc(sketch, "E59.0.1.5", {"start": v(-29.44, 5.8) * mm, "mid": v(-28.92, 4.53) * mm, "end": v(-27.64, 4) * mm});
            skLineSegment(sketch, "E59.0.1.6", {"start": v(-27.64, 4) * mm, "end": v(-27.24, 4) * mm});
            skArc(sketch, "E59.0.1.7", {"start": v(-27.24, 4) * mm, "mid": v(-25.97, 4.53) * mm, "end": v(-25.44, 5.8) * mm});
            skLineSegment(sketch, "E59.1.0.0", {"start": v(-21.34, 46) * mm, "end": v(-20.94, 46) * mm});
            skArc(sketch, "E59.1.0.1", {"start": v(-19.14, 44.2) * mm, "mid": v(-19.67, 45.47) * mm, "end": v(-20.94, 46) * mm});
            skLineSegment(sketch, "E59.1.0.2", {"start": v(-19.14, 44.2) * mm, "end": v(-19.14, 28.05) * mm});
            skArc(sketch, "E59.1.0.3", {"start": v(-21.34, 46) * mm, "mid": v(-22.62, 45.47) * mm, "end": v(-23.14, 44.2) * mm});
            skLineSegment(sketch, "E59.1.0.4", {"start": v(-23.14, 44.2) * mm, "end": v(-23.14, 28.05) * mm});
            skArc(sketch, "E59.1.0.5", {"start": v(-23.14, 28.05) * mm, "mid": v(-22.62, 26.78) * mm, "end": v(-21.34, 26.25) * mm});
            skLineSegment(sketch, "E59.1.0.6", {"start": v(-21.34, 26.25) * mm, "end": v(-20.94, 26.25) * mm});
            skArc(sketch, "E59.1.0.7", {"start": v(-20.94, 26.25) * mm, "mid": v(-19.67, 26.78) * mm, "end": v(-19.14, 28.05) * mm});
            skLineSegment(sketch, "E59.1.1.0", {"start": v(-21.34, 23.75) * mm, "end": v(-20.94, 23.75) * mm});
            skArc(sketch, "E59.1.1.1", {"start": v(-19.14, 21.95) * mm, "mid": v(-19.67, 23.22) * mm, "end": v(-20.94, 23.75) * mm});
            skLineSegment(sketch, "E59.1.1.2", {"start": v(-19.14, 21.95) * mm, "end": v(-19.14, 5.8) * mm});
            skArc(sketch, "E59.1.1.3", {"start": v(-21.34, 23.75) * mm, "mid": v(-22.62, 23.22) * mm, "end": v(-23.14, 21.95) * mm});
            skLineSegment(sketch, "E59.1.1.4", {"start": v(-23.14, 21.95) * mm, "end": v(-23.14, 5.8) * mm});
            skArc(sketch, "E59.1.1.5", {"start": v(-23.14, 5.8) * mm, "mid": v(-22.62, 4.53) * mm, "end": v(-21.34, 4) * mm});
            skLineSegment(sketch, "E59.1.1.6", {"start": v(-21.34, 4) * mm, "end": v(-20.94, 4) * mm});
            skArc(sketch, "E59.1.1.7", {"start": v(-20.94, 4) * mm, "mid": v(-19.67, 4.53) * mm, "end": v(-19.14, 5.8) * mm});
            skLineSegment(sketch, "E59.2.0.0", {"start": v(-15.04, 46) * mm, "end": v(-14.64, 46) * mm});
            skArc(sketch, "E59.2.0.1", {"start": v(-12.84, 44.2) * mm, "mid": v(-13.37, 45.47) * mm, "end": v(-14.64, 46) * mm});
            skLineSegment(sketch, "E59.2.0.2", {"start": v(-12.84, 44.2) * mm, "end": v(-12.84, 28.05) * mm});
            skArc(sketch, "E59.2.0.3", {"start": v(-15.04, 46) * mm, "mid": v(-16.32, 45.47) * mm, "end": v(-16.84, 44.2) * mm});
            skLineSegment(sketch, "E59.2.0.4", {"start": v(-16.84, 44.2) * mm, "end": v(-16.84, 28.05) * mm});
            skArc(sketch, "E59.2.0.5", {"start": v(-16.84, 28.05) * mm, "mid": v(-16.32, 26.78) * mm, "end": v(-15.04, 26.25) * mm});
            skLineSegment(sketch, "E59.2.0.6", {"start": v(-15.04, 26.25) * mm, "end": v(-14.64, 26.25) * mm});
            skArc(sketch, "E59.2.0.7", {"start": v(-14.64, 26.25) * mm, "mid": v(-13.37, 26.78) * mm, "end": v(-12.84, 28.05) * mm});
            skLineSegment(sketch, "E59.2.1.0", {"start": v(-15.04, 23.75) * mm, "end": v(-14.64, 23.75) * mm});
            skArc(sketch, "E59.2.1.1", {"start": v(-12.84, 21.95) * mm, "mid": v(-13.37, 23.22) * mm, "end": v(-14.64, 23.75) * mm});
            skLineSegment(sketch, "E59.2.1.2", {"start": v(-12.84, 21.95) * mm, "end": v(-12.84, 5.8) * mm});
            skArc(sketch, "E59.2.1.3", {"start": v(-15.04, 23.75) * mm, "mid": v(-16.32, 23.22) * mm, "end": v(-16.84, 21.95) * mm});
            skLineSegment(sketch, "E59.2.1.4", {"start": v(-16.84, 21.95) * mm, "end": v(-16.84, 5.8) * mm});
            skArc(sketch, "E59.2.1.5", {"start": v(-16.84, 5.8) * mm, "mid": v(-16.32, 4.53) * mm, "end": v(-15.04, 4) * mm});
            skLineSegment(sketch, "E59.2.1.6", {"start": v(-15.04, 4) * mm, "end": v(-14.64, 4) * mm});
            skArc(sketch, "E59.2.1.7", {"start": v(-14.64, 4) * mm, "mid": v(-13.37, 4.53) * mm, "end": v(-12.84, 5.8) * mm});
            skLineSegment(sketch, "E59.3.0.0", {"start": v(-8.74, 46) * mm, "end": v(-8.34, 46) * mm});
            skArc(sketch, "E59.3.0.1", {"start": v(-6.54, 44.2) * mm, "mid": v(-7.07, 45.47) * mm, "end": v(-8.34, 46) * mm});
            skLineSegment(sketch, "E59.3.0.2", {"start": v(-6.54, 44.2) * mm, "end": v(-6.54, 28.05) * mm});
            skArc(sketch, "E59.3.0.3", {"start": v(-8.74, 46) * mm, "mid": v(-10.02, 45.47) * mm, "end": v(-10.54, 44.2) * mm});
            skLineSegment(sketch, "E59.3.0.4", {"start": v(-10.54, 44.2) * mm, "end": v(-10.54, 28.05) * mm});
            skArc(sketch, "E59.3.0.5", {"start": v(-10.54, 28.05) * mm, "mid": v(-10.02, 26.78) * mm, "end": v(-8.74, 26.25) * mm});
            skLineSegment(sketch, "E59.3.0.6", {"start": v(-8.74, 26.25) * mm, "end": v(-8.34, 26.25) * mm});
            skArc(sketch, "E59.3.0.7", {"start": v(-8.34, 26.25) * mm, "mid": v(-7.07, 26.78) * mm, "end": v(-6.54, 28.05) * mm});
            skLineSegment(sketch, "E59.3.1.0", {"start": v(-8.74, 23.75) * mm, "end": v(-8.34, 23.75) * mm});
            skArc(sketch, "E59.3.1.1", {"start": v(-6.54, 21.95) * mm, "mid": v(-7.07, 23.22) * mm, "end": v(-8.34, 23.75) * mm});
            skLineSegment(sketch, "E59.3.1.2", {"start": v(-6.54, 21.95) * mm, "end": v(-6.54, 5.8) * mm});
            skArc(sketch, "E59.3.1.3", {"start": v(-8.74, 23.75) * mm, "mid": v(-10.02, 23.22) * mm, "end": v(-10.54, 21.95) * mm});
            skLineSegment(sketch, "E59.3.1.4", {"start": v(-10.54, 21.95) * mm, "end": v(-10.54, 5.8) * mm});
            skArc(sketch, "E59.3.1.5", {"start": v(-10.54, 5.8) * mm, "mid": v(-10.02, 4.53) * mm, "end": v(-8.74, 4) * mm});
            skLineSegment(sketch, "E59.3.1.6", {"start": v(-8.74, 4) * mm, "end": v(-8.34, 4) * mm});
            skArc(sketch, "E59.3.1.7", {"start": v(-8.34, 4) * mm, "mid": v(-7.07, 4.53) * mm, "end": v(-6.54, 5.8) * mm});
            skLineSegment(sketch, "E59.4.0.0", {"start": v(-2.44, 46) * mm, "end": v(-2.04, 46) * mm});
            skArc(sketch, "E59.4.0.1", {"start": v(-0.24, 44.2) * mm, "mid": v(-0.77, 45.47) * mm, "end": v(-2.04, 46) * mm});
            skLineSegment(sketch, "E59.4.0.2", {"start": v(-0.24, 44.2) * mm, "end": v(-0.24, 28.05) * mm});
            skArc(sketch, "E59.4.0.3", {"start": v(-2.44, 46) * mm, "mid": v(-3.72, 45.47) * mm, "end": v(-4.24, 44.2) * mm});
            skLineSegment(sketch, "E59.4.0.4", {"start": v(-4.24, 44.2) * mm, "end": v(-4.24, 28.05) * mm});
            skArc(sketch, "E59.4.0.5", {"start": v(-4.24, 28.05) * mm, "mid": v(-3.72, 26.78) * mm, "end": v(-2.44, 26.25) * mm});
            skLineSegment(sketch, "E59.4.0.6", {"start": v(-2.44, 26.25) * mm, "end": v(-2.04, 26.25) * mm});
            skArc(sketch, "E59.4.0.7", {"start": v(-2.04, 26.25) * mm, "mid": v(-0.77, 26.78) * mm, "end": v(-0.24, 28.05) * mm});
            skLineSegment(sketch, "E59.4.1.0", {"start": v(-2.44, 23.75) * mm, "end": v(-2.04, 23.75) * mm});
            skArc(sketch, "E59.4.1.1", {"start": v(-0.24, 21.95) * mm, "mid": v(-0.77, 23.22) * mm, "end": v(-2.04, 23.75) * mm});
            skLineSegment(sketch, "E59.4.1.2", {"start": v(-0.24, 21.95) * mm, "end": v(-0.24, 5.8) * mm});
            skArc(sketch, "E59.4.1.3", {"start": v(-2.44, 23.75) * mm, "mid": v(-3.72, 23.22) * mm, "end": v(-4.24, 21.95) * mm});
            skLineSegment(sketch, "E59.4.1.4", {"start": v(-4.24, 21.95) * mm, "end": v(-4.24, 5.8) * mm});
            skArc(sketch, "E59.4.1.5", {"start": v(-4.24, 5.8) * mm, "mid": v(-3.72, 4.53) * mm, "end": v(-2.44, 4) * mm});
            skLineSegment(sketch, "E59.4.1.6", {"start": v(-2.44, 4) * mm, "end": v(-2.04, 4) * mm});
            skArc(sketch, "E59.4.1.7", {"start": v(-2.04, 4) * mm, "mid": v(-0.77, 4.53) * mm, "end": v(-0.24, 5.8) * mm});
            skLineSegment(sketch, "E59.5.0.0", {"start": v(3.86, 46) * mm, "end": v(4.26, 46) * mm});
            skArc(sketch, "E59.5.0.1", {"start": v(6.06, 44.2) * mm, "mid": v(5.53, 45.47) * mm, "end": v(4.26, 46) * mm});
            skLineSegment(sketch, "E59.5.0.2", {"start": v(6.06, 44.2) * mm, "end": v(6.06, 28.05) * mm});
            skArc(sketch, "E59.5.0.3", {"start": v(3.86, 46) * mm, "mid": v(2.58, 45.47) * mm, "end": v(2.06, 44.2) * mm});
            skLineSegment(sketch, "E59.5.0.4", {"start": v(2.06, 44.2) * mm, "end": v(2.06, 28.05) * mm});
            skArc(sketch, "E59.5.0.5", {"start": v(2.06, 28.05) * mm, "mid": v(2.58, 26.78) * mm, "end": v(3.86, 26.25) * mm});
            skLineSegment(sketch, "E59.5.0.6", {"start": v(3.86, 26.25) * mm, "end": v(4.26, 26.25) * mm});
            skArc(sketch, "E59.5.0.7", {"start": v(4.26, 26.25) * mm, "mid": v(5.53, 26.78) * mm, "end": v(6.06, 28.05) * mm});
            skLineSegment(sketch, "E59.5.1.0", {"start": v(3.86, 23.75) * mm, "end": v(4.26, 23.75) * mm});
            skArc(sketch, "E59.5.1.1", {"start": v(6.06, 21.95) * mm, "mid": v(5.53, 23.22) * mm, "end": v(4.26, 23.75) * mm});
            skLineSegment(sketch, "E59.5.1.2", {"start": v(6.06, 21.95) * mm, "end": v(6.06, 5.8) * mm});
            skArc(sketch, "E59.5.1.3", {"start": v(3.86, 23.75) * mm, "mid": v(2.58, 23.22) * mm, "end": v(2.06, 21.95) * mm});
            skLineSegment(sketch, "E59.5.1.4", {"start": v(2.06, 21.95) * mm, "end": v(2.06, 5.8) * mm});
            skArc(sketch, "E59.5.1.5", {"start": v(2.06, 5.8) * mm, "mid": v(2.58, 4.53) * mm, "end": v(3.86, 4) * mm});
            skLineSegment(sketch, "E59.5.1.6", {"start": v(3.86, 4) * mm, "end": v(4.26, 4) * mm});
            skArc(sketch, "E59.5.1.7", {"start": v(4.26, 4) * mm, "mid": v(5.53, 4.53) * mm, "end": v(6.06, 5.8) * mm});
            skLineSegment(sketch, "E59.6.0.0", {"start": v(10.16, 46) * mm, "end": v(10.56, 46) * mm});
            skArc(sketch, "E59.6.0.1", {"start": v(12.36, 44.2) * mm, "mid": v(11.83, 45.47) * mm, "end": v(10.56, 46) * mm});
            skLineSegment(sketch, "E59.6.0.2", {"start": v(12.36, 44.2) * mm, "end": v(12.36, 28.05) * mm});
            skArc(sketch, "E59.6.0.3", {"start": v(10.16, 46) * mm, "mid": v(8.88, 45.47) * mm, "end": v(8.36, 44.2) * mm});
            skLineSegment(sketch, "E59.6.0.4", {"start": v(8.36, 44.2) * mm, "end": v(8.36, 28.05) * mm});
            skArc(sketch, "E59.6.0.5", {"start": v(8.36, 28.05) * mm, "mid": v(8.88, 26.78) * mm, "end": v(10.16, 26.25) * mm});
            skLineSegment(sketch, "E59.6.0.6", {"start": v(10.16, 26.25) * mm, "end": v(10.56, 26.25) * mm});
            skArc(sketch, "E59.6.0.7", {"start": v(10.56, 26.25) * mm, "mid": v(11.83, 26.78) * mm, "end": v(12.36, 28.05) * mm});
            skLineSegment(sketch, "E59.6.1.0", {"start": v(10.16, 23.75) * mm, "end": v(10.56, 23.75) * mm});
            skArc(sketch, "E59.6.1.1", {"start": v(12.36, 21.95) * mm, "mid": v(11.83, 23.22) * mm, "end": v(10.56, 23.75) * mm});
            skLineSegment(sketch, "E59.6.1.2", {"start": v(12.36, 21.95) * mm, "end": v(12.36, 5.8) * mm});
            skArc(sketch, "E59.6.1.3", {"start": v(10.16, 23.75) * mm, "mid": v(8.88, 23.22) * mm, "end": v(8.36, 21.95) * mm});
            skLineSegment(sketch, "E59.6.1.4", {"start": v(8.36, 21.95) * mm, "end": v(8.36, 5.8) * mm});
            skArc(sketch, "E59.6.1.5", {"start": v(8.36, 5.8) * mm, "mid": v(8.88, 4.53) * mm, "end": v(10.16, 4) * mm});
            skLineSegment(sketch, "E59.6.1.6", {"start": v(10.16, 4) * mm, "end": v(10.56, 4) * mm});
            skArc(sketch, "E59.6.1.7", {"start": v(10.56, 4) * mm, "mid": v(11.83, 4.53) * mm, "end": v(12.36, 5.8) * mm});
            skLineSegment(sketch, "E59.7.0.0", {"start": v(16.46, 46) * mm, "end": v(16.86, 46) * mm});
            skArc(sketch, "E59.7.0.1", {"start": v(18.66, 44.2) * mm, "mid": v(18.13, 45.47) * mm, "end": v(16.86, 46) * mm});
            skLineSegment(sketch, "E59.7.0.2", {"start": v(18.66, 44.2) * mm, "end": v(18.66, 28.05) * mm});
            skArc(sketch, "E59.7.0.3", {"start": v(16.46, 46) * mm, "mid": v(15.18, 45.47) * mm, "end": v(14.66, 44.2) * mm});
            skLineSegment(sketch, "E59.7.0.4", {"start": v(14.66, 44.2) * mm, "end": v(14.66, 28.05) * mm});
            skArc(sketch, "E59.7.0.5", {"start": v(14.66, 28.05) * mm, "mid": v(15.18, 26.78) * mm, "end": v(16.46, 26.25) * mm});
            skLineSegment(sketch, "E59.7.0.6", {"start": v(16.46, 26.25) * mm, "end": v(16.86, 26.25) * mm});
            skArc(sketch, "E59.7.0.7", {"start": v(16.86, 26.25) * mm, "mid": v(18.13, 26.78) * mm, "end": v(18.66, 28.05) * mm});
            skLineSegment(sketch, "E59.7.1.0", {"start": v(16.46, 23.75) * mm, "end": v(16.86, 23.75) * mm});
            skArc(sketch, "E59.7.1.1", {"start": v(18.66, 21.95) * mm, "mid": v(18.13, 23.22) * mm, "end": v(16.86, 23.75) * mm});
            skLineSegment(sketch, "E59.7.1.2", {"start": v(18.66, 21.95) * mm, "end": v(18.66, 5.8) * mm});
            skArc(sketch, "E59.7.1.3", {"start": v(16.46, 23.75) * mm, "mid": v(15.18, 23.22) * mm, "end": v(14.66, 21.95) * mm});
            skLineSegment(sketch, "E59.7.1.4", {"start": v(14.66, 21.95) * mm, "end": v(14.66, 5.8) * mm});
            skArc(sketch, "E59.7.1.5", {"start": v(14.66, 5.8) * mm, "mid": v(15.18, 4.53) * mm, "end": v(16.46, 4) * mm});
            skLineSegment(sketch, "E59.7.1.6", {"start": v(16.46, 4) * mm, "end": v(16.86, 4) * mm});
            skArc(sketch, "E59.7.1.7", {"start": v(16.86, 4) * mm, "mid": v(18.13, 4.53) * mm, "end": v(18.66, 5.8) * mm});
            skLineSegment(sketch, "E59.8.0.0", {"start": v(22.76, 46) * mm, "end": v(23.16, 46) * mm});
            skArc(sketch, "E59.8.0.1", {"start": v(24.96, 44.2) * mm, "mid": v(24.43, 45.47) * mm, "end": v(23.16, 46) * mm});
            skLineSegment(sketch, "E59.8.0.2", {"start": v(24.96, 44.2) * mm, "end": v(24.96, 28.05) * mm});
            skArc(sketch, "E59.8.0.3", {"start": v(22.76, 46) * mm, "mid": v(21.48, 45.47) * mm, "end": v(20.96, 44.2) * mm});
            skLineSegment(sketch, "E59.8.0.4", {"start": v(20.96, 44.2) * mm, "end": v(20.96, 28.05) * mm});
            skArc(sketch, "E59.8.0.5", {"start": v(20.96, 28.05) * mm, "mid": v(21.48, 26.78) * mm, "end": v(22.76, 26.25) * mm});
            skLineSegment(sketch, "E59.8.0.6", {"start": v(22.76, 26.25) * mm, "end": v(23.16, 26.25) * mm});
            skArc(sketch, "E59.8.0.7", {"start": v(23.16, 26.25) * mm, "mid": v(24.43, 26.78) * mm, "end": v(24.96, 28.05) * mm});
            skLineSegment(sketch, "E59.8.1.0", {"start": v(22.76, 23.75) * mm, "end": v(23.16, 23.75) * mm});
            skArc(sketch, "E59.8.1.1", {"start": v(24.96, 21.95) * mm, "mid": v(24.43, 23.22) * mm, "end": v(23.16, 23.75) * mm});
            skLineSegment(sketch, "E59.8.1.2", {"start": v(24.96, 21.95) * mm, "end": v(24.96, 5.8) * mm});
            skArc(sketch, "E59.8.1.3", {"start": v(22.76, 23.75) * mm, "mid": v(21.48, 23.22) * mm, "end": v(20.96, 21.95) * mm});
            skLineSegment(sketch, "E59.8.1.4", {"start": v(20.96, 21.95) * mm, "end": v(20.96, 5.8) * mm});
            skArc(sketch, "E59.8.1.5", {"start": v(20.96, 5.8) * mm, "mid": v(21.48, 4.53) * mm, "end": v(22.76, 4) * mm});
            skLineSegment(sketch, "E59.8.1.6", {"start": v(22.76, 4) * mm, "end": v(23.16, 4) * mm});
            skArc(sketch, "E59.8.1.7", {"start": v(23.16, 4) * mm, "mid": v(24.43, 4.53) * mm, "end": v(24.96, 5.8) * mm});
            skLineSegment(sketch, "E59.9.0.0", {"start": v(29.06, 46) * mm, "end": v(29.46, 46) * mm});
            skArc(sketch, "E59.9.0.1", {"start": v(31.26, 44.2) * mm, "mid": v(30.73, 45.47) * mm, "end": v(29.46, 46) * mm});
            skLineSegment(sketch, "E59.9.0.2", {"start": v(31.26, 44.2) * mm, "end": v(31.26, 28.05) * mm});
            skArc(sketch, "E59.9.0.3", {"start": v(29.06, 46) * mm, "mid": v(27.78, 45.47) * mm, "end": v(27.26, 44.2) * mm});
            skLineSegment(sketch, "E59.9.0.4", {"start": v(27.26, 44.2) * mm, "end": v(27.26, 28.05) * mm});
            skArc(sketch, "E59.9.0.5", {"start": v(27.26, 28.05) * mm, "mid": v(27.78, 26.78) * mm, "end": v(29.06, 26.25) * mm});
            skLineSegment(sketch, "E59.9.0.6", {"start": v(29.06, 26.25) * mm, "end": v(29.46, 26.25) * mm});
            skArc(sketch, "E59.9.0.7", {"start": v(29.46, 26.25) * mm, "mid": v(30.73, 26.78) * mm, "end": v(31.26, 28.05) * mm});
            skLineSegment(sketch, "E59.9.1.0", {"start": v(29.06, 23.75) * mm, "end": v(29.46, 23.75) * mm});
            skArc(sketch, "E59.9.1.1", {"start": v(31.26, 21.95) * mm, "mid": v(30.73, 23.22) * mm, "end": v(29.46, 23.75) * mm});
            skLineSegment(sketch, "E59.9.1.2", {"start": v(31.26, 21.95) * mm, "end": v(31.26, 5.8) * mm});
            skArc(sketch, "E59.9.1.3", {"start": v(29.06, 23.75) * mm, "mid": v(27.78, 23.22) * mm, "end": v(27.26, 21.95) * mm});
            skLineSegment(sketch, "E59.9.1.4", {"start": v(27.26, 21.95) * mm, "end": v(27.26, 5.8) * mm});
            skArc(sketch, "E59.9.1.5", {"start": v(27.26, 5.8) * mm, "mid": v(27.78, 4.53) * mm, "end": v(29.06, 4) * mm});
            skLineSegment(sketch, "E59.9.1.6", {"start": v(29.06, 4) * mm, "end": v(29.46, 4) * mm});
            skArc(sketch, "E59.9.1.7", {"start": v(29.46, 4) * mm, "mid": v(30.73, 4.53) * mm, "end": v(31.26, 5.8) * mm});
            skLineSegment(sketch, "E59.10.0.0", {"start": v(35.36, 46) * mm, "end": v(35.76, 46) * mm});
            skArc(sketch, "E59.10.0.1", {"start": v(37.56, 44.2) * mm, "mid": v(37.03, 45.47) * mm, "end": v(35.76, 46) * mm});
            skLineSegment(sketch, "E59.10.0.2", {"start": v(37.56, 44.2) * mm, "end": v(37.56, 28.05) * mm});
            skArc(sketch, "E59.10.0.3", {"start": v(35.36, 46) * mm, "mid": v(34.08, 45.47) * mm, "end": v(33.56, 44.2) * mm});
            skLineSegment(sketch, "E59.10.0.4", {"start": v(33.56, 44.2) * mm, "end": v(33.56, 28.05) * mm});
            skArc(sketch, "E59.10.0.5", {"start": v(33.56, 28.05) * mm, "mid": v(34.08, 26.78) * mm, "end": v(35.36, 26.25) * mm});
            skLineSegment(sketch, "E59.10.0.6", {"start": v(35.36, 26.25) * mm, "end": v(35.76, 26.25) * mm});
            skArc(sketch, "E59.10.0.7", {"start": v(35.76, 26.25) * mm, "mid": v(37.03, 26.78) * mm, "end": v(37.56, 28.05) * mm});
            skLineSegment(sketch, "E59.10.1.0", {"start": v(35.36, 23.75) * mm, "end": v(35.76, 23.75) * mm});
            skArc(sketch, "E59.10.1.1", {"start": v(37.56, 21.95) * mm, "mid": v(37.03, 23.22) * mm, "end": v(35.76, 23.75) * mm});
            skLineSegment(sketch, "E59.10.1.2", {"start": v(37.56, 21.95) * mm, "end": v(37.56, 5.8) * mm});
            skArc(sketch, "E59.10.1.3", {"start": v(35.36, 23.75) * mm, "mid": v(34.08, 23.22) * mm, "end": v(33.56, 21.95) * mm});
            skLineSegment(sketch, "E59.10.1.4", {"start": v(33.56, 21.95) * mm, "end": v(33.56, 5.8) * mm});
            skArc(sketch, "E59.10.1.5", {"start": v(33.56, 5.8) * mm, "mid": v(34.08, 4.53) * mm, "end": v(35.36, 4) * mm});
            skLineSegment(sketch, "E59.10.1.6", {"start": v(35.36, 4) * mm, "end": v(35.76, 4) * mm});
            skArc(sketch, "E59.10.1.7", {"start": v(35.76, 4) * mm, "mid": v(37.03, 4.53) * mm, "end": v(37.56, 5.8) * mm});
            skLineSegment(sketch, "E59.11.0.0", {"start": v(41.66, 46) * mm, "end": v(42.06, 46) * mm});
            skArc(sketch, "E59.11.0.1", {"start": v(43.86, 44.2) * mm, "mid": v(43.33, 45.47) * mm, "end": v(42.06, 46) * mm});
            skLineSegment(sketch, "E59.11.0.2", {"start": v(43.86, 44.2) * mm, "end": v(43.86, 28.05) * mm});
            skArc(sketch, "E59.11.0.3", {"start": v(41.66, 46) * mm, "mid": v(40.38, 45.47) * mm, "end": v(39.86, 44.2) * mm});
            skLineSegment(sketch, "E59.11.0.4", {"start": v(39.86, 44.2) * mm, "end": v(39.86, 28.05) * mm});
            skArc(sketch, "E59.11.0.5", {"start": v(39.86, 28.05) * mm, "mid": v(40.38, 26.78) * mm, "end": v(41.66, 26.25) * mm});
            skLineSegment(sketch, "E59.11.0.6", {"start": v(41.66, 26.25) * mm, "end": v(42.06, 26.25) * mm});
            skArc(sketch, "E59.11.0.7", {"start": v(42.06, 26.25) * mm, "mid": v(43.33, 26.78) * mm, "end": v(43.86, 28.05) * mm});
            skLineSegment(sketch, "E59.11.1.0", {"start": v(41.66, 23.75) * mm, "end": v(42.06, 23.75) * mm});
            skArc(sketch, "E59.11.1.1", {"start": v(43.86, 21.95) * mm, "mid": v(43.33, 23.22) * mm, "end": v(42.06, 23.75) * mm});
            skLineSegment(sketch, "E59.11.1.2", {"start": v(43.86, 21.95) * mm, "end": v(43.86, 5.8) * mm});
            skArc(sketch, "E59.11.1.3", {"start": v(41.66, 23.75) * mm, "mid": v(40.38, 23.22) * mm, "end": v(39.86, 21.95) * mm});
            skLineSegment(sketch, "E59.11.1.4", {"start": v(39.86, 21.95) * mm, "end": v(39.86, 5.8) * mm});
            skArc(sketch, "E59.11.1.5", {"start": v(39.86, 5.8) * mm, "mid": v(40.38, 4.53) * mm, "end": v(41.66, 4) * mm});
            skLineSegment(sketch, "E59.11.1.6", {"start": v(41.66, 4) * mm, "end": v(42.06, 4) * mm});
            skArc(sketch, "E59.11.1.7", {"start": v(42.06, 4) * mm, "mid": v(43.33, 4.53) * mm, "end": v(43.86, 5.8) * mm});
            skLineSegment(sketch, "E59.12.0.0", {"start": v(47.96, 46) * mm, "end": v(48.36, 46) * mm});
            skArc(sketch, "E59.12.0.1", {"start": v(50.16, 44.2) * mm, "mid": v(49.63, 45.47) * mm, "end": v(48.36, 46) * mm});
            skLineSegment(sketch, "E59.12.0.2", {"start": v(50.16, 44.2) * mm, "end": v(50.16, 28.05) * mm});
            skArc(sketch, "E59.12.0.3", {"start": v(47.96, 46) * mm, "mid": v(46.68, 45.47) * mm, "end": v(46.16, 44.2) * mm});
            skLineSegment(sketch, "E59.12.0.4", {"start": v(46.16, 44.2) * mm, "end": v(46.16, 28.05) * mm});
            skArc(sketch, "E59.12.0.5", {"start": v(46.16, 28.05) * mm, "mid": v(46.68, 26.78) * mm, "end": v(47.96, 26.25) * mm});
            skLineSegment(sketch, "E59.12.0.6", {"start": v(47.96, 26.25) * mm, "end": v(48.36, 26.25) * mm});
            skArc(sketch, "E59.12.0.7", {"start": v(48.36, 26.25) * mm, "mid": v(49.63, 26.78) * mm, "end": v(50.16, 28.05) * mm});
            skLineSegment(sketch, "E59.12.1.0", {"start": v(47.96, 23.75) * mm, "end": v(48.36, 23.75) * mm});
            skArc(sketch, "E59.12.1.1", {"start": v(50.16, 21.95) * mm, "mid": v(49.63, 23.22) * mm, "end": v(48.36, 23.75) * mm});
            skLineSegment(sketch, "E59.12.1.2", {"start": v(50.16, 21.95) * mm, "end": v(50.16, 5.8) * mm});
            skArc(sketch, "E59.12.1.3", {"start": v(47.96, 23.75) * mm, "mid": v(46.68, 23.22) * mm, "end": v(46.16, 21.95) * mm});
            skLineSegment(sketch, "E59.12.1.4", {"start": v(46.16, 21.95) * mm, "end": v(46.16, 5.8) * mm});
            skArc(sketch, "E59.12.1.5", {"start": v(46.16, 5.8) * mm, "mid": v(46.68, 4.53) * mm, "end": v(47.96, 4) * mm});
            skLineSegment(sketch, "E59.12.1.6", {"start": v(47.96, 4) * mm, "end": v(48.36, 4) * mm});
            skArc(sketch, "E59.12.1.7", {"start": v(48.36, 4) * mm, "mid": v(49.63, 4.53) * mm, "end": v(50.16, 5.8) * mm});
            skLineSegment(sketch, "E59.13.0.0", {"start": v(54.26, 46) * mm, "end": v(54.66, 46) * mm});
            skArc(sketch, "E59.13.0.1", {"start": v(56.46, 44.2) * mm, "mid": v(55.93, 45.47) * mm, "end": v(54.66, 46) * mm});
            skLineSegment(sketch, "E59.13.0.2", {"start": v(56.46, 44.2) * mm, "end": v(56.46, 28.05) * mm});
            skArc(sketch, "E59.13.0.3", {"start": v(54.26, 46) * mm, "mid": v(52.98, 45.47) * mm, "end": v(52.46, 44.2) * mm});
            skLineSegment(sketch, "E59.13.0.4", {"start": v(52.46, 44.2) * mm, "end": v(52.46, 28.05) * mm});
            skArc(sketch, "E59.13.0.5", {"start": v(52.46, 28.05) * mm, "mid": v(52.98, 26.78) * mm, "end": v(54.26, 26.25) * mm});
            skLineSegment(sketch, "E59.13.0.6", {"start": v(54.26, 26.25) * mm, "end": v(54.66, 26.25) * mm});
            skArc(sketch, "E59.13.0.7", {"start": v(54.66, 26.25) * mm, "mid": v(55.93, 26.78) * mm, "end": v(56.46, 28.05) * mm});
            skLineSegment(sketch, "E59.13.1.0", {"start": v(54.26, 23.75) * mm, "end": v(54.66, 23.75) * mm});
            skArc(sketch, "E59.13.1.1", {"start": v(56.46, 21.95) * mm, "mid": v(55.93, 23.22) * mm, "end": v(54.66, 23.75) * mm});
            skLineSegment(sketch, "E59.13.1.2", {"start": v(56.46, 21.95) * mm, "end": v(56.46, 5.8) * mm});
            skArc(sketch, "E59.13.1.3", {"start": v(54.26, 23.75) * mm, "mid": v(52.98, 23.22) * mm, "end": v(52.46, 21.95) * mm});
            skLineSegment(sketch, "E59.13.1.4", {"start": v(52.46, 21.95) * mm, "end": v(52.46, 5.8) * mm});
            skArc(sketch, "E59.13.1.5", {"start": v(52.46, 5.8) * mm, "mid": v(52.98, 4.53) * mm, "end": v(54.26, 4) * mm});
            skLineSegment(sketch, "E59.13.1.6", {"start": v(54.26, 4) * mm, "end": v(54.66, 4) * mm});
            skArc(sketch, "E59.13.1.7", {"start": v(54.66, 4) * mm, "mid": v(55.93, 4.53) * mm, "end": v(56.46, 5.8) * mm});
            skLineSegment(sketch, "E59.14.0.0", {"start": v(60.56, 46) * mm, "end": v(60.96, 46) * mm});
            skArc(sketch, "E59.14.0.1", {"start": v(62.76, 44.2) * mm, "mid": v(62.23, 45.47) * mm, "end": v(60.96, 46) * mm});
            skLineSegment(sketch, "E59.14.0.2", {"start": v(62.76, 44.2) * mm, "end": v(62.76, 28.05) * mm});
            skArc(sketch, "E59.14.0.3", {"start": v(60.56, 46) * mm, "mid": v(59.28, 45.47) * mm, "end": v(58.76, 44.2) * mm});
            skLineSegment(sketch, "E59.14.0.4", {"start": v(58.76, 44.2) * mm, "end": v(58.76, 28.05) * mm});
            skArc(sketch, "E59.14.0.5", {"start": v(58.76, 28.05) * mm, "mid": v(59.28, 26.78) * mm, "end": v(60.56, 26.25) * mm});
            skLineSegment(sketch, "E59.14.0.6", {"start": v(60.56, 26.25) * mm, "end": v(60.96, 26.25) * mm});
            skArc(sketch, "E59.14.0.7", {"start": v(60.96, 26.25) * mm, "mid": v(62.23, 26.78) * mm, "end": v(62.76, 28.05) * mm});
            skLineSegment(sketch, "E59.14.1.0", {"start": v(60.56, 23.75) * mm, "end": v(60.96, 23.75) * mm});
            skArc(sketch, "E59.14.1.1", {"start": v(62.76, 21.95) * mm, "mid": v(62.23, 23.22) * mm, "end": v(60.96, 23.75) * mm});
            skLineSegment(sketch, "E59.14.1.2", {"start": v(62.76, 21.95) * mm, "end": v(62.76, 5.8) * mm});
            skArc(sketch, "E59.14.1.3", {"start": v(60.56, 23.75) * mm, "mid": v(59.28, 23.22) * mm, "end": v(58.76, 21.95) * mm});
            skLineSegment(sketch, "E59.14.1.4", {"start": v(58.76, 21.95) * mm, "end": v(58.76, 5.8) * mm});
            skArc(sketch, "E59.14.1.5", {"start": v(58.76, 5.8) * mm, "mid": v(59.28, 4.53) * mm, "end": v(60.56, 4) * mm});
            skLineSegment(sketch, "E59.14.1.6", {"start": v(60.56, 4) * mm, "end": v(60.96, 4) * mm});
            skArc(sketch, "E59.14.1.7", {"start": v(60.96, 4) * mm, "mid": v(62.23, 4.53) * mm, "end": v(62.76, 5.8) * mm});
            skLineSegment(sketch, "E59.direction1", {"start": v(-27.64, 46) * mm, "end": v(-21.34, 46) * mm, "construction": true});
            skLineSegment(sketch, "E59.direction2", {"start": v(-27.64, 46) * mm, "end": v(-27.64, 23.75) * mm, "construction": true});
            skSolve(sketch);
        }
        {
            var Q0;
            Q0=makeQuery(id+"F17.imprint","IMPRINT",FACE,{"disambiguationData":[TD([[makeQuery(id+"F17.imprint","IMPRINT",EDGE,{"derivedFrom":sQuery(id+"F17.wireOp",EDGE,"E54.bottom")}),-1.0]])]});
            var Q1;
            Q1=makeQuery(id+"F17.imprint","IMPRINT",FACE,{"disambiguationData":[TD([[makeQuery(id+"F17.imprint","IMPRINT",EDGE,{"derivedFrom":sQuery(id+"F17.wireOp",EDGE,"E59.1.0.0")}),-1.0]])]});
            var Q2;
            Q2=makeQuery(id+"F17.imprint","IMPRINT",FACE,{"disambiguationData":[TD([[makeQuery(id+"F17.imprint","IMPRINT",EDGE,{"derivedFrom":sQuery(id+"F17.wireOp",EDGE,"E59.2.0.0")}),-1.0]])]});
            var Q3;
            Q3=makeQuery(id+"F17.imprint","IMPRINT",FACE,{"disambiguationData":[TD([[makeQuery(id+"F17.imprint","IMPRINT",EDGE,{"derivedFrom":sQuery(id+"F17.wireOp",EDGE,"E59.3.0.0")}),-1.0]])]});
            var Q4;
            Q4=makeQuery(id+"F17.imprint","IMPRINT",FACE,{"disambiguationData":[TD([[makeQuery(id+"F17.imprint","IMPRINT",EDGE,{"derivedFrom":sQuery(id+"F17.wireOp",EDGE,"E59.4.0.0")}),-1.0]])]});
            var Q5;
            Q5=makeQuery(id+"F17.imprint","IMPRINT",FACE,{"disambiguationData":[TD([[makeQuery(id+"F17.imprint","IMPRINT",EDGE,{"derivedFrom":sQuery(id+"F17.wireOp",EDGE,"E59.5.0.0")}),-1.0]])]});
            var Q6;
            Q6=makeQuery(id+"F17.imprint","IMPRINT",FACE,{"disambiguationData":[TD([[makeQuery(id+"F17.imprint","IMPRINT",EDGE,{"derivedFrom":sQuery(id+"F17.wireOp",EDGE,"E59.6.0.0")}),-1.0]])]});
            var Q7;
            Q7=makeQuery(id+"F17.imprint","IMPRINT",FACE,{"disambiguationData":[TD([[makeQuery(id+"F17.imprint","IMPRINT",EDGE,{"derivedFrom":sQuery(id+"F17.wireOp",EDGE,"E59.7.0.0")}),-1.0]])]});
            var Q8;
            Q8=makeQuery(id+"F17.imprint","IMPRINT",FACE,{"disambiguationData":[TD([[makeQuery(id+"F17.imprint","IMPRINT",EDGE,{"derivedFrom":sQuery(id+"F17.wireOp",EDGE,"E59.8.0.0")}),-1.0]])]});
            var Q9;
            Q9=makeQuery(id+"F17.imprint","IMPRINT",FACE,{"disambiguationData":[TD([[makeQuery(id+"F17.imprint","IMPRINT",EDGE,{"derivedFrom":sQuery(id+"F17.wireOp",EDGE,"E59.9.0.0")}),-1.0]])]});
            var Q10;
            Q10=makeQuery(id+"F17.imprint","IMPRINT",FACE,{"disambiguationData":[TD([[makeQuery(id+"F17.imprint","IMPRINT",EDGE,{"derivedFrom":sQuery(id+"F17.wireOp",EDGE,"E59.10.0.0")}),-1.0]])]});
            var Q11;
            Q11=makeQuery(id+"F17.imprint","IMPRINT",FACE,{"disambiguationData":[TD([[makeQuery(id+"F17.imprint","IMPRINT",EDGE,{"derivedFrom":sQuery(id+"F17.wireOp",EDGE,"E59.11.0.0")}),-1.0]])]});
            var Q12;
            Q12=makeQuery(id+"F17.imprint","IMPRINT",FACE,{"disambiguationData":[TD([[makeQuery(id+"F17.imprint","IMPRINT",EDGE,{"derivedFrom":sQuery(id+"F17.wireOp",EDGE,"E59.12.0.0")}),-1.0]])]});
            var Q13;
            Q13=makeQuery(id+"F17.imprint","IMPRINT",FACE,{"disambiguationData":[TD([[makeQuery(id+"F17.imprint","IMPRINT",EDGE,{"derivedFrom":sQuery(id+"F17.wireOp",EDGE,"E59.13.0.0")}),-1.0]])]});
            var Q14;
            Q14=makeQuery(id+"F17.imprint","IMPRINT",FACE,{"disambiguationData":[TD([[makeQuery(id+"F17.imprint","IMPRINT",EDGE,{"derivedFrom":sQuery(id+"F17.wireOp",EDGE,"E59.14.0.0")}),-1.0]])]});
            var Q15;
            Q15=makeQuery(id+"F17.imprint","IMPRINT",FACE,{"disambiguationData":[TD([[makeQuery(id+"F17.imprint","IMPRINT",EDGE,{"derivedFrom":sQuery(id+"F17.wireOp",EDGE,"E59.0.1.0")}),-1.0]])]});
            var Q16;
            Q16=makeQuery(id+"F17.imprint","IMPRINT",FACE,{"disambiguationData":[TD([[makeQuery(id+"F17.imprint","IMPRINT",EDGE,{"derivedFrom":sQuery(id+"F17.wireOp",EDGE,"E59.1.1.0")}),-1.0]])]});
            var Q17;
            Q17=makeQuery(id+"F17.imprint","IMPRINT",FACE,{"disambiguationData":[TD([[makeQuery(id+"F17.imprint","IMPRINT",EDGE,{"derivedFrom":sQuery(id+"F17.wireOp",EDGE,"E59.2.1.0")}),-1.0]])]});
            var Q18;
            Q18=makeQuery(id+"F17.imprint","IMPRINT",FACE,{"disambiguationData":[TD([[makeQuery(id+"F17.imprint","IMPRINT",EDGE,{"derivedFrom":sQuery(id+"F17.wireOp",EDGE,"E59.3.1.0")}),-1.0]])]});
            var Q19;
            Q19=makeQuery(id+"F17.imprint","IMPRINT",FACE,{"disambiguationData":[TD([[makeQuery(id+"F17.imprint","IMPRINT",EDGE,{"derivedFrom":sQuery(id+"F17.wireOp",EDGE,"E59.4.1.0")}),-1.0]])]});
            var Q20;
            Q20=makeQuery(id+"F17.imprint","IMPRINT",FACE,{"disambiguationData":[TD([[makeQuery(id+"F17.imprint","IMPRINT",EDGE,{"derivedFrom":sQuery(id+"F17.wireOp",EDGE,"E59.5.1.0")}),-1.0]])]});
            var Q21;
            Q21=makeQuery(id+"F17.imprint","IMPRINT",FACE,{"disambiguationData":[TD([[makeQuery(id+"F17.imprint","IMPRINT",EDGE,{"derivedFrom":sQuery(id+"F17.wireOp",EDGE,"E59.6.1.0")}),-1.0]])]});
            var Q22;
            Q22=makeQuery(id+"F17.imprint","IMPRINT",FACE,{"disambiguationData":[TD([[makeQuery(id+"F17.imprint","IMPRINT",EDGE,{"derivedFrom":sQuery(id+"F17.wireOp",EDGE,"E59.7.1.0")}),-1.0]])]});
            var Q23;
            Q23=makeQuery(id+"F17.imprint","IMPRINT",FACE,{"disambiguationData":[TD([[makeQuery(id+"F17.imprint","IMPRINT",EDGE,{"derivedFrom":sQuery(id+"F17.wireOp",EDGE,"E59.8.1.0")}),-1.0]])]});
            var Q24;
            Q24=makeQuery(id+"F17.imprint","IMPRINT",FACE,{"disambiguationData":[TD([[makeQuery(id+"F17.imprint","IMPRINT",EDGE,{"derivedFrom":sQuery(id+"F17.wireOp",EDGE,"E59.9.1.0")}),-1.0]])]});
            var Q25;
            Q25=makeQuery(id+"F17.imprint","IMPRINT",FACE,{"disambiguationData":[TD([[makeQuery(id+"F17.imprint","IMPRINT",EDGE,{"derivedFrom":sQuery(id+"F17.wireOp",EDGE,"E59.10.1.0")}),-1.0]])]});
            var Q26;
            Q26=makeQuery(id+"F17.imprint","IMPRINT",FACE,{"disambiguationData":[TD([[makeQuery(id+"F17.imprint","IMPRINT",EDGE,{"derivedFrom":sQuery(id+"F17.wireOp",EDGE,"E59.11.1.0")}),-1.0]])]});
            var Q27;
            Q27=makeQuery(id+"F17.imprint","IMPRINT",FACE,{"disambiguationData":[TD([[makeQuery(id+"F17.imprint","IMPRINT",EDGE,{"derivedFrom":sQuery(id+"F17.wireOp",EDGE,"E59.12.1.0")}),-1.0]])]});
            var Q28;
            Q28=makeQuery(id+"F17.imprint","IMPRINT",FACE,{"disambiguationData":[TD([[makeQuery(id+"F17.imprint","IMPRINT",EDGE,{"derivedFrom":sQuery(id+"F17.wireOp",EDGE,"E59.13.1.0")}),-1.0]])]});
            var Q29;
            Q29=makeQuery(id+"F17.imprint","IMPRINT",FACE,{"disambiguationData":[TD([[makeQuery(id+"F17.imprint","IMPRINT",EDGE,{"derivedFrom":sQuery(id+"F17.wireOp",EDGE,"E59.14.1.0")}),-1.0]])]});
            extrude(context, id + "F18", {"entities" : qUnion([Q0, Q1, Q2, Q3, Q4, Q5, Q6, Q7, Q8, Q9, Q10, Q11, Q12, Q13, Q14, Q15, Q16, Q17, Q18, Q19, Q20, Q21, Q22, Q23, Q24, Q25, Q26, Q27, Q28, Q29]), "operationType" : NewBodyOperationType.REMOVE, "endBound" : BoundingType.THROUGH_ALL, "oppositeDirection" : true, "depth" : 25 * mm, "offsetDistance" : 25 * mm});
        }
        {
            var Q0;
            Q0=makeQuery(id+"F3.opExtrude","SWEPT_FACE",FACE,{"disambiguationData":[OSD([sQuery(id+"F2.wireOp",EDGE,"E44.0")])]});
            var sketch = newSketch(context, id + "F19", { "sketchPlane" : qUnion([Q0])});
            skLineSegment(sketch, "E60.bottom", {"start": v(-21.8, 46) * mm, "end": v(-21.4, 46) * mm});
            skLineSegment(sketch, "E60.top", {"start": v(-21.8, 31.5) * mm, "end": v(-21.4, 31.5) * mm});
            skLineSegment(sketch, "E60.left", {"start": v(-23.6, 44.2) * mm, "end": v(-23.6, 33.3) * mm});
            skLineSegment(sketch, "E60.right", {"start": v(-19.6, 44.2) * mm, "end": v(-19.6, 33.3) * mm});
            skPoint(sketch, "E61.visualSharp", {"position": v(-23.6, 46) * mm});
            skArc(sketch, "E61.filletArc", {"start": v(-21.8, 46) * mm, "mid": v(-23.07, 45.47) * mm, "end": v(-23.6, 44.2) * mm});
            skPoint(sketch, "E62.visualSharp", {"position": v(-19.6, 46) * mm});
            skArc(sketch, "E62.filletArc", {"start": v(-19.6, 44.2) * mm, "mid": v(-20.13, 45.47) * mm, "end": v(-21.4, 46) * mm});
            skPoint(sketch, "E63.visualSharp", {"position": v(-23.6, 31.5) * mm});
            skArc(sketch, "E63.filletArc", {"start": v(-23.6, 33.3) * mm, "mid": v(-23.07, 32.03) * mm, "end": v(-21.8, 31.5) * mm});
            skPoint(sketch, "E64.visualSharp", {"position": v(-19.6, 31.5) * mm});
            skArc(sketch, "E64.filletArc", {"start": v(-21.4, 31.5) * mm, "mid": v(-20.13, 32.03) * mm, "end": v(-19.6, 33.3) * mm});
            skArc(sketch, "E65.0.1.0", {"start": v(-19.6, 26.2) * mm, "mid": v(-20.13, 27.47) * mm, "end": v(-21.4, 28) * mm});
            skLineSegment(sketch, "E65.0.1.1", {"start": v(-19.6, 26.2) * mm, "end": v(-19.6, 15.3) * mm});
            skArc(sketch, "E65.0.1.2", {"start": v(-21.4, 13.5) * mm, "mid": v(-20.13, 14.03) * mm, "end": v(-19.6, 15.3) * mm});
            skLineSegment(sketch, "E65.0.1.3", {"start": v(-21.8, 13.5) * mm, "end": v(-21.4, 13.5) * mm});
            skArc(sketch, "E65.0.1.4", {"start": v(-23.6, 15.3) * mm, "mid": v(-23.07, 14.03) * mm, "end": v(-21.8, 13.5) * mm});
            skLineSegment(sketch, "E65.0.1.5", {"start": v(-23.6, 26.2) * mm, "end": v(-23.6, 15.3) * mm});
            skArc(sketch, "E65.0.1.6", {"start": v(-21.8, 28) * mm, "mid": v(-23.07, 27.47) * mm, "end": v(-23.6, 26.2) * mm});
            skLineSegment(sketch, "E65.0.1.7", {"start": v(-21.8, 28) * mm, "end": v(-21.4, 28) * mm});
            skArc(sketch, "E65.1.0.0", {"start": v(-13.4, 44.2) * mm, "mid": v(-13.93, 45.47) * mm, "end": v(-15.2, 46) * mm});
            skLineSegment(sketch, "E65.1.0.1", {"start": v(-13.4, 44.2) * mm, "end": v(-13.4, 33.3) * mm});
            skArc(sketch, "E65.1.0.2", {"start": v(-15.2, 31.5) * mm, "mid": v(-13.93, 32.03) * mm, "end": v(-13.4, 33.3) * mm});
            skLineSegment(sketch, "E65.1.0.3", {"start": v(-15.6, 31.5) * mm, "end": v(-15.2, 31.5) * mm});
            skArc(sketch, "E65.1.0.4", {"start": v(-17.4, 33.3) * mm, "mid": v(-16.87, 32.03) * mm, "end": v(-15.6, 31.5) * mm});
            skLineSegment(sketch, "E65.1.0.5", {"start": v(-17.4, 44.2) * mm, "end": v(-17.4, 33.3) * mm});
            skArc(sketch, "E65.1.0.6", {"start": v(-15.6, 46) * mm, "mid": v(-16.87, 45.47) * mm, "end": v(-17.4, 44.2) * mm});
            skLineSegment(sketch, "E65.1.0.7", {"start": v(-15.6, 46) * mm, "end": v(-15.2, 46) * mm});
            skArc(sketch, "E65.1.1.0", {"start": v(-13.4, 26.2) * mm, "mid": v(-13.93, 27.47) * mm, "end": v(-15.2, 28) * mm});
            skLineSegment(sketch, "E65.1.1.1", {"start": v(-13.4, 26.2) * mm, "end": v(-13.4, 15.3) * mm});
            skArc(sketch, "E65.1.1.2", {"start": v(-15.2, 13.5) * mm, "mid": v(-13.93, 14.03) * mm, "end": v(-13.4, 15.3) * mm});
            skLineSegment(sketch, "E65.1.1.3", {"start": v(-15.6, 13.5) * mm, "end": v(-15.2, 13.5) * mm});
            skArc(sketch, "E65.1.1.4", {"start": v(-17.4, 15.3) * mm, "mid": v(-16.87, 14.03) * mm, "end": v(-15.6, 13.5) * mm});
            skLineSegment(sketch, "E65.1.1.5", {"start": v(-17.4, 26.2) * mm, "end": v(-17.4, 15.3) * mm});
            skArc(sketch, "E65.1.1.6", {"start": v(-15.6, 28) * mm, "mid": v(-16.87, 27.47) * mm, "end": v(-17.4, 26.2) * mm});
            skLineSegment(sketch, "E65.1.1.7", {"start": v(-15.6, 28) * mm, "end": v(-15.2, 28) * mm});
            skArc(sketch, "E65.2.0.0", {"start": v(-7.2, 44.2) * mm, "mid": v(-7.73, 45.47) * mm, "end": v(-9, 46) * mm});
            skLineSegment(sketch, "E65.2.0.1", {"start": v(-7.2, 44.2) * mm, "end": v(-7.2, 33.3) * mm});
            skArc(sketch, "E65.2.0.2", {"start": v(-9, 31.5) * mm, "mid": v(-7.73, 32.03) * mm, "end": v(-7.2, 33.3) * mm});
            skLineSegment(sketch, "E65.2.0.3", {"start": v(-9.4, 31.5) * mm, "end": v(-9, 31.5) * mm});
            skArc(sketch, "E65.2.0.4", {"start": v(-11.2, 33.3) * mm, "mid": v(-10.67, 32.03) * mm, "end": v(-9.4, 31.5) * mm});
            skLineSegment(sketch, "E65.2.0.5", {"start": v(-11.2, 44.2) * mm, "end": v(-11.2, 33.3) * mm});
            skArc(sketch, "E65.2.0.6", {"start": v(-9.4, 46) * mm, "mid": v(-10.67, 45.47) * mm, "end": v(-11.2, 44.2) * mm});
            skLineSegment(sketch, "E65.2.0.7", {"start": v(-9.4, 46) * mm, "end": v(-9, 46) * mm});
            skArc(sketch, "E65.2.1.0", {"start": v(-7.2, 26.2) * mm, "mid": v(-7.73, 27.47) * mm, "end": v(-9, 28) * mm});
            skLineSegment(sketch, "E65.2.1.1", {"start": v(-7.2, 26.2) * mm, "end": v(-7.2, 15.3) * mm});
            skArc(sketch, "E65.2.1.2", {"start": v(-9, 13.5) * mm, "mid": v(-7.73, 14.03) * mm, "end": v(-7.2, 15.3) * mm});
            skLineSegment(sketch, "E65.2.1.3", {"start": v(-9.4, 13.5) * mm, "end": v(-9, 13.5) * mm});
            skArc(sketch, "E65.2.1.4", {"start": v(-11.2, 15.3) * mm, "mid": v(-10.67, 14.03) * mm, "end": v(-9.4, 13.5) * mm});
            skLineSegment(sketch, "E65.2.1.5", {"start": v(-11.2, 26.2) * mm, "end": v(-11.2, 15.3) * mm});
            skArc(sketch, "E65.2.1.6", {"start": v(-9.4, 28) * mm, "mid": v(-10.67, 27.47) * mm, "end": v(-11.2, 26.2) * mm});
            skLineSegment(sketch, "E65.2.1.7", {"start": v(-9.4, 28) * mm, "end": v(-9, 28) * mm});
            skArc(sketch, "E65.3.0.0", {"start": v(-1, 44.2) * mm, "mid": v(-1.53, 45.47) * mm, "end": v(-2.8, 46) * mm});
            skLineSegment(sketch, "E65.3.0.1", {"start": v(-1, 44.2) * mm, "end": v(-1, 33.3) * mm});
            skArc(sketch, "E65.3.0.2", {"start": v(-2.8, 31.5) * mm, "mid": v(-1.53, 32.03) * mm, "end": v(-1, 33.3) * mm});
            skLineSegment(sketch, "E65.3.0.3", {"start": v(-3.2, 31.5) * mm, "end": v(-2.8, 31.5) * mm});
            skArc(sketch, "E65.3.0.4", {"start": v(-5, 33.3) * mm, "mid": v(-4.47, 32.03) * mm, "end": v(-3.2, 31.5) * mm});
            skLineSegment(sketch, "E65.3.0.5", {"start": v(-5, 44.2) * mm, "end": v(-5, 33.3) * mm});
            skArc(sketch, "E65.3.0.6", {"start": v(-3.2, 46) * mm, "mid": v(-4.47, 45.47) * mm, "end": v(-5, 44.2) * mm});
            skLineSegment(sketch, "E65.3.0.7", {"start": v(-3.2, 46) * mm, "end": v(-2.8, 46) * mm});
            skArc(sketch, "E65.3.1.0", {"start": v(-1, 26.2) * mm, "mid": v(-1.53, 27.47) * mm, "end": v(-2.8, 28) * mm});
            skLineSegment(sketch, "E65.3.1.1", {"start": v(-1, 26.2) * mm, "end": v(-1, 15.3) * mm});
            skArc(sketch, "E65.3.1.2", {"start": v(-2.8, 13.5) * mm, "mid": v(-1.53, 14.03) * mm, "end": v(-1, 15.3) * mm});
            skLineSegment(sketch, "E65.3.1.3", {"start": v(-3.2, 13.5) * mm, "end": v(-2.8, 13.5) * mm});
            skArc(sketch, "E65.3.1.4", {"start": v(-5, 15.3) * mm, "mid": v(-4.47, 14.03) * mm, "end": v(-3.2, 13.5) * mm});
            skLineSegment(sketch, "E65.3.1.5", {"start": v(-5, 26.2) * mm, "end": v(-5, 15.3) * mm});
            skArc(sketch, "E65.3.1.6", {"start": v(-3.2, 28) * mm, "mid": v(-4.47, 27.47) * mm, "end": v(-5, 26.2) * mm});
            skLineSegment(sketch, "E65.3.1.7", {"start": v(-3.2, 28) * mm, "end": v(-2.8, 28) * mm});
            skArc(sketch, "E65.4.0.0", {"start": v(5.2, 44.2) * mm, "mid": v(4.67, 45.47) * mm, "end": v(3.4, 46) * mm});
            skLineSegment(sketch, "E65.4.0.1", {"start": v(5.2, 44.2) * mm, "end": v(5.2, 33.3) * mm});
            skArc(sketch, "E65.4.0.2", {"start": v(3.4, 31.5) * mm, "mid": v(4.67, 32.03) * mm, "end": v(5.2, 33.3) * mm});
            skLineSegment(sketch, "E65.4.0.3", {"start": v(3, 31.5) * mm, "end": v(3.4, 31.5) * mm});
            skArc(sketch, "E65.4.0.4", {"start": v(1.2, 33.3) * mm, "mid": v(1.73, 32.03) * mm, "end": v(3, 31.5) * mm});
            skLineSegment(sketch, "E65.4.0.5", {"start": v(1.2, 44.2) * mm, "end": v(1.2, 33.3) * mm});
            skArc(sketch, "E65.4.0.6", {"start": v(3, 46) * mm, "mid": v(1.73, 45.47) * mm, "end": v(1.2, 44.2) * mm});
            skLineSegment(sketch, "E65.4.0.7", {"start": v(3, 46) * mm, "end": v(3.4, 46) * mm});
            skArc(sketch, "E65.4.1.0", {"start": v(5.2, 26.2) * mm, "mid": v(4.67, 27.47) * mm, "end": v(3.4, 28) * mm});
            skLineSegment(sketch, "E65.4.1.1", {"start": v(5.2, 26.2) * mm, "end": v(5.2, 15.3) * mm});
            skArc(sketch, "E65.4.1.2", {"start": v(3.4, 13.5) * mm, "mid": v(4.67, 14.03) * mm, "end": v(5.2, 15.3) * mm});
            skLineSegment(sketch, "E65.4.1.3", {"start": v(3, 13.5) * mm, "end": v(3.4, 13.5) * mm});
            skArc(sketch, "E65.4.1.4", {"start": v(1.2, 15.3) * mm, "mid": v(1.73, 14.03) * mm, "end": v(3, 13.5) * mm});
            skLineSegment(sketch, "E65.4.1.5", {"start": v(1.2, 26.2) * mm, "end": v(1.2, 15.3) * mm});
            skArc(sketch, "E65.4.1.6", {"start": v(3, 28) * mm, "mid": v(1.73, 27.47) * mm, "end": v(1.2, 26.2) * mm});
            skLineSegment(sketch, "E65.4.1.7", {"start": v(3, 28) * mm, "end": v(3.4, 28) * mm});
            skArc(sketch, "E65.5.0.0", {"start": v(11.4, 44.2) * mm, "mid": v(10.87, 45.47) * mm, "end": v(9.6, 46) * mm});
            skLineSegment(sketch, "E65.5.0.1", {"start": v(11.4, 44.2) * mm, "end": v(11.4, 33.3) * mm});
            skArc(sketch, "E65.5.0.2", {"start": v(9.6, 31.5) * mm, "mid": v(10.87, 32.03) * mm, "end": v(11.4, 33.3) * mm});
            skLineSegment(sketch, "E65.5.0.3", {"start": v(9.2, 31.5) * mm, "end": v(9.6, 31.5) * mm});
            skArc(sketch, "E65.5.0.4", {"start": v(7.4, 33.3) * mm, "mid": v(7.93, 32.03) * mm, "end": v(9.2, 31.5) * mm});
            skLineSegment(sketch, "E65.5.0.5", {"start": v(7.4, 44.2) * mm, "end": v(7.4, 33.3) * mm});
            skArc(sketch, "E65.5.0.6", {"start": v(9.2, 46) * mm, "mid": v(7.93, 45.47) * mm, "end": v(7.4, 44.2) * mm});
            skLineSegment(sketch, "E65.5.0.7", {"start": v(9.2, 46) * mm, "end": v(9.6, 46) * mm});
            skArc(sketch, "E65.5.1.0", {"start": v(11.4, 26.2) * mm, "mid": v(10.87, 27.47) * mm, "end": v(9.6, 28) * mm});
            skLineSegment(sketch, "E65.5.1.1", {"start": v(11.4, 26.2) * mm, "end": v(11.4, 15.3) * mm});
            skArc(sketch, "E65.5.1.2", {"start": v(9.6, 13.5) * mm, "mid": v(10.87, 14.03) * mm, "end": v(11.4, 15.3) * mm});
            skLineSegment(sketch, "E65.5.1.3", {"start": v(9.2, 13.5) * mm, "end": v(9.6, 13.5) * mm});
            skArc(sketch, "E65.5.1.4", {"start": v(7.4, 15.3) * mm, "mid": v(7.93, 14.03) * mm, "end": v(9.2, 13.5) * mm});
            skLineSegment(sketch, "E65.5.1.5", {"start": v(7.4, 26.2) * mm, "end": v(7.4, 15.3) * mm});
            skArc(sketch, "E65.5.1.6", {"start": v(9.2, 28) * mm, "mid": v(7.93, 27.47) * mm, "end": v(7.4, 26.2) * mm});
            skLineSegment(sketch, "E65.5.1.7", {"start": v(9.2, 28) * mm, "end": v(9.6, 28) * mm});
            skArc(sketch, "E65.6.0.0", {"start": v(17.6, 44.2) * mm, "mid": v(17.07, 45.47) * mm, "end": v(15.8, 46) * mm});
            skLineSegment(sketch, "E65.6.0.1", {"start": v(17.6, 44.2) * mm, "end": v(17.6, 33.3) * mm});
            skArc(sketch, "E65.6.0.2", {"start": v(15.8, 31.5) * mm, "mid": v(17.07, 32.03) * mm, "end": v(17.6, 33.3) * mm});
            skLineSegment(sketch, "E65.6.0.3", {"start": v(15.4, 31.5) * mm, "end": v(15.8, 31.5) * mm});
            skArc(sketch, "E65.6.0.4", {"start": v(13.6, 33.3) * mm, "mid": v(14.13, 32.03) * mm, "end": v(15.4, 31.5) * mm});
            skLineSegment(sketch, "E65.6.0.5", {"start": v(13.6, 44.2) * mm, "end": v(13.6, 33.3) * mm});
            skArc(sketch, "E65.6.0.6", {"start": v(15.4, 46) * mm, "mid": v(14.13, 45.47) * mm, "end": v(13.6, 44.2) * mm});
            skLineSegment(sketch, "E65.6.0.7", {"start": v(15.4, 46) * mm, "end": v(15.8, 46) * mm});
            skArc(sketch, "E65.6.1.0", {"start": v(17.6, 26.2) * mm, "mid": v(17.07, 27.47) * mm, "end": v(15.8, 28) * mm});
            skLineSegment(sketch, "E65.6.1.1", {"start": v(17.6, 26.2) * mm, "end": v(17.6, 15.3) * mm});
            skArc(sketch, "E65.6.1.2", {"start": v(15.8, 13.5) * mm, "mid": v(17.07, 14.03) * mm, "end": v(17.6, 15.3) * mm});
            skLineSegment(sketch, "E65.6.1.3", {"start": v(15.4, 13.5) * mm, "end": v(15.8, 13.5) * mm});
            skArc(sketch, "E65.6.1.4", {"start": v(13.6, 15.3) * mm, "mid": v(14.13, 14.03) * mm, "end": v(15.4, 13.5) * mm});
            skLineSegment(sketch, "E65.6.1.5", {"start": v(13.6, 26.2) * mm, "end": v(13.6, 15.3) * mm});
            skArc(sketch, "E65.6.1.6", {"start": v(15.4, 28) * mm, "mid": v(14.13, 27.47) * mm, "end": v(13.6, 26.2) * mm});
            skLineSegment(sketch, "E65.6.1.7", {"start": v(15.4, 28) * mm, "end": v(15.8, 28) * mm});
            skArc(sketch, "E65.7.0.0", {"start": v(23.8, 44.2) * mm, "mid": v(23.27, 45.47) * mm, "end": v(22, 46) * mm});
            skLineSegment(sketch, "E65.7.0.1", {"start": v(23.8, 44.2) * mm, "end": v(23.8, 33.3) * mm});
            skArc(sketch, "E65.7.0.2", {"start": v(22, 31.5) * mm, "mid": v(23.27, 32.03) * mm, "end": v(23.8, 33.3) * mm});
            skLineSegment(sketch, "E65.7.0.3", {"start": v(21.6, 31.5) * mm, "end": v(22, 31.5) * mm});
            skArc(sketch, "E65.7.0.4", {"start": v(19.8, 33.3) * mm, "mid": v(20.33, 32.03) * mm, "end": v(21.6, 31.5) * mm});
            skLineSegment(sketch, "E65.7.0.5", {"start": v(19.8, 44.2) * mm, "end": v(19.8, 33.3) * mm});
            skArc(sketch, "E65.7.0.6", {"start": v(21.6, 46) * mm, "mid": v(20.33, 45.47) * mm, "end": v(19.8, 44.2) * mm});
            skLineSegment(sketch, "E65.7.0.7", {"start": v(21.6, 46) * mm, "end": v(22, 46) * mm});
            skArc(sketch, "E65.7.1.0", {"start": v(23.8, 26.2) * mm, "mid": v(23.27, 27.47) * mm, "end": v(22, 28) * mm});
            skLineSegment(sketch, "E65.7.1.1", {"start": v(23.8, 26.2) * mm, "end": v(23.8, 15.3) * mm});
            skArc(sketch, "E65.7.1.2", {"start": v(22, 13.5) * mm, "mid": v(23.27, 14.03) * mm, "end": v(23.8, 15.3) * mm});
            skLineSegment(sketch, "E65.7.1.3", {"start": v(21.6, 13.5) * mm, "end": v(22, 13.5) * mm});
            skArc(sketch, "E65.7.1.4", {"start": v(19.8, 15.3) * mm, "mid": v(20.33, 14.03) * mm, "end": v(21.6, 13.5) * mm});
            skLineSegment(sketch, "E65.7.1.5", {"start": v(19.8, 26.2) * mm, "end": v(19.8, 15.3) * mm});
            skArc(sketch, "E65.7.1.6", {"start": v(21.6, 28) * mm, "mid": v(20.33, 27.47) * mm, "end": v(19.8, 26.2) * mm});
            skLineSegment(sketch, "E65.7.1.7", {"start": v(21.6, 28) * mm, "end": v(22, 28) * mm});
            skArc(sketch, "E65.8.0.0", {"start": v(30, 44.2) * mm, "mid": v(29.47, 45.47) * mm, "end": v(28.2, 46) * mm});
            skLineSegment(sketch, "E65.8.0.1", {"start": v(30, 44.2) * mm, "end": v(30, 33.3) * mm});
            skArc(sketch, "E65.8.0.2", {"start": v(28.2, 31.5) * mm, "mid": v(29.47, 32.03) * mm, "end": v(30, 33.3) * mm});
            skLineSegment(sketch, "E65.8.0.3", {"start": v(27.8, 31.5) * mm, "end": v(28.2, 31.5) * mm});
            skArc(sketch, "E65.8.0.4", {"start": v(26, 33.3) * mm, "mid": v(26.53, 32.03) * mm, "end": v(27.8, 31.5) * mm});
            skLineSegment(sketch, "E65.8.0.5", {"start": v(26, 44.2) * mm, "end": v(26, 33.3) * mm});
            skArc(sketch, "E65.8.0.6", {"start": v(27.8, 46) * mm, "mid": v(26.53, 45.47) * mm, "end": v(26, 44.2) * mm});
            skLineSegment(sketch, "E65.8.0.7", {"start": v(27.8, 46) * mm, "end": v(28.2, 46) * mm});
            skArc(sketch, "E65.8.1.0", {"start": v(30, 26.2) * mm, "mid": v(29.47, 27.47) * mm, "end": v(28.2, 28) * mm});
            skLineSegment(sketch, "E65.8.1.1", {"start": v(30, 26.2) * mm, "end": v(30, 15.3) * mm});
            skArc(sketch, "E65.8.1.2", {"start": v(28.2, 13.5) * mm, "mid": v(29.47, 14.03) * mm, "end": v(30, 15.3) * mm});
            skLineSegment(sketch, "E65.8.1.3", {"start": v(27.8, 13.5) * mm, "end": v(28.2, 13.5) * mm});
            skArc(sketch, "E65.8.1.4", {"start": v(26, 15.3) * mm, "mid": v(26.53, 14.03) * mm, "end": v(27.8, 13.5) * mm});
            skLineSegment(sketch, "E65.8.1.5", {"start": v(26, 26.2) * mm, "end": v(26, 15.3) * mm});
            skArc(sketch, "E65.8.1.6", {"start": v(27.8, 28) * mm, "mid": v(26.53, 27.47) * mm, "end": v(26, 26.2) * mm});
            skLineSegment(sketch, "E65.8.1.7", {"start": v(27.8, 28) * mm, "end": v(28.2, 28) * mm});
            skArc(sketch, "E65.9.0.0", {"start": v(36.2, 44.2) * mm, "mid": v(35.67, 45.47) * mm, "end": v(34.4, 46) * mm});
            skLineSegment(sketch, "E65.9.0.1", {"start": v(36.2, 44.2) * mm, "end": v(36.2, 33.3) * mm});
            skArc(sketch, "E65.9.0.2", {"start": v(34.4, 31.5) * mm, "mid": v(35.67, 32.03) * mm, "end": v(36.2, 33.3) * mm});
            skLineSegment(sketch, "E65.9.0.3", {"start": v(34, 31.5) * mm, "end": v(34.4, 31.5) * mm});
            skArc(sketch, "E65.9.0.4", {"start": v(32.2, 33.3) * mm, "mid": v(32.73, 32.03) * mm, "end": v(34, 31.5) * mm});
            skLineSegment(sketch, "E65.9.0.5", {"start": v(32.2, 44.2) * mm, "end": v(32.2, 33.3) * mm});
            skArc(sketch, "E65.9.0.6", {"start": v(34, 46) * mm, "mid": v(32.73, 45.47) * mm, "end": v(32.2, 44.2) * mm});
            skLineSegment(sketch, "E65.9.0.7", {"start": v(34, 46) * mm, "end": v(34.4, 46) * mm});
            skArc(sketch, "E65.9.1.0", {"start": v(36.2, 26.2) * mm, "mid": v(35.67, 27.47) * mm, "end": v(34.4, 28) * mm});
            skLineSegment(sketch, "E65.9.1.1", {"start": v(36.2, 26.2) * mm, "end": v(36.2, 15.3) * mm});
            skArc(sketch, "E65.9.1.2", {"start": v(34.4, 13.5) * mm, "mid": v(35.67, 14.03) * mm, "end": v(36.2, 15.3) * mm});
            skLineSegment(sketch, "E65.9.1.3", {"start": v(34, 13.5) * mm, "end": v(34.4, 13.5) * mm});
            skArc(sketch, "E65.9.1.4", {"start": v(32.2, 15.3) * mm, "mid": v(32.73, 14.03) * mm, "end": v(34, 13.5) * mm});
            skLineSegment(sketch, "E65.9.1.5", {"start": v(32.2, 26.2) * mm, "end": v(32.2, 15.3) * mm});
            skArc(sketch, "E65.9.1.6", {"start": v(34, 28) * mm, "mid": v(32.73, 27.47) * mm, "end": v(32.2, 26.2) * mm});
            skLineSegment(sketch, "E65.9.1.7", {"start": v(34, 28) * mm, "end": v(34.4, 28) * mm});
            skLineSegment(sketch, "E65.direction1", {"start": v(-21.4, 44.2) * mm, "end": v(-15.2, 44.2) * mm, "construction": true});
            skLineSegment(sketch, "E65.direction2", {"start": v(-21.4, 44.2) * mm, "end": v(-21.4, 26.2) * mm, "construction": true});
            skSolve(sketch);
        }
        {
            var Q0;
            Q0=makeQuery(id+"F19.imprint","IMPRINT",FACE,{"disambiguationData":[TD([[makeQuery(id+"F19.imprint","IMPRINT",EDGE,{"derivedFrom":sQuery(id+"F19.wireOp",EDGE,"E60.bottom")}),-1.0]])]});
            var Q1;
            Q1=makeQuery(id+"F19.imprint","IMPRINT",FACE,{"disambiguationData":[TD([[makeQuery(id+"F19.imprint","IMPRINT",EDGE,{"derivedFrom":sQuery(id+"F19.wireOp",EDGE,"E65.1.0.0")}),1.0]])]});
            var Q2;
            Q2=makeQuery(id+"F19.imprint","IMPRINT",FACE,{"disambiguationData":[TD([[makeQuery(id+"F19.imprint","IMPRINT",EDGE,{"derivedFrom":sQuery(id+"F19.wireOp",EDGE,"E65.2.0.0")}),1.0]])]});
            var Q3;
            Q3=makeQuery(id+"F19.imprint","IMPRINT",FACE,{"disambiguationData":[TD([[makeQuery(id+"F19.imprint","IMPRINT",EDGE,{"derivedFrom":sQuery(id+"F19.wireOp",EDGE,"E65.3.0.0")}),1.0]])]});
            var Q4;
            Q4=makeQuery(id+"F19.imprint","IMPRINT",FACE,{"disambiguationData":[TD([[makeQuery(id+"F19.imprint","IMPRINT",EDGE,{"derivedFrom":sQuery(id+"F19.wireOp",EDGE,"E65.4.0.0")}),1.0]])]});
            var Q5;
            Q5=makeQuery(id+"F19.imprint","IMPRINT",FACE,{"disambiguationData":[TD([[makeQuery(id+"F19.imprint","IMPRINT",EDGE,{"derivedFrom":sQuery(id+"F19.wireOp",EDGE,"E65.5.0.0")}),1.0]])]});
            var Q6;
            Q6=makeQuery(id+"F19.imprint","IMPRINT",FACE,{"disambiguationData":[TD([[makeQuery(id+"F19.imprint","IMPRINT",EDGE,{"derivedFrom":sQuery(id+"F19.wireOp",EDGE,"E65.6.0.0")}),1.0]])]});
            var Q7;
            Q7=makeQuery(id+"F19.imprint","IMPRINT",FACE,{"disambiguationData":[TD([[makeQuery(id+"F19.imprint","IMPRINT",EDGE,{"derivedFrom":sQuery(id+"F19.wireOp",EDGE,"E65.7.0.0")}),1.0]])]});
            var Q8;
            Q8=makeQuery(id+"F19.imprint","IMPRINT",FACE,{"disambiguationData":[TD([[makeQuery(id+"F19.imprint","IMPRINT",EDGE,{"derivedFrom":sQuery(id+"F19.wireOp",EDGE,"E65.8.0.0")}),1.0]])]});
            var Q9;
            Q9=makeQuery(id+"F19.imprint","IMPRINT",FACE,{"disambiguationData":[TD([[makeQuery(id+"F19.imprint","IMPRINT",EDGE,{"derivedFrom":sQuery(id+"F19.wireOp",EDGE,"E65.9.0.0")}),1.0]])]});
            var Q10;
            Q10=makeQuery(id+"F19.imprint","IMPRINT",FACE,{"disambiguationData":[TD([[makeQuery(id+"F19.imprint","IMPRINT",EDGE,{"derivedFrom":sQuery(id+"F19.wireOp",EDGE,"E65.0.1.0")}),1.0]])]});
            var Q11;
            Q11=makeQuery(id+"F19.imprint","IMPRINT",FACE,{"disambiguationData":[TD([[makeQuery(id+"F19.imprint","IMPRINT",EDGE,{"derivedFrom":sQuery(id+"F19.wireOp",EDGE,"E65.1.1.0")}),1.0]])]});
            var Q12;
            Q12=makeQuery(id+"F19.imprint","IMPRINT",FACE,{"disambiguationData":[TD([[makeQuery(id+"F19.imprint","IMPRINT",EDGE,{"derivedFrom":sQuery(id+"F19.wireOp",EDGE,"E65.2.1.0")}),1.0]])]});
            var Q13;
            Q13=makeQuery(id+"F19.imprint","IMPRINT",FACE,{"disambiguationData":[TD([[makeQuery(id+"F19.imprint","IMPRINT",EDGE,{"derivedFrom":sQuery(id+"F19.wireOp",EDGE,"E65.3.1.0")}),1.0]])]});
            var Q14;
            Q14=makeQuery(id+"F19.imprint","IMPRINT",FACE,{"disambiguationData":[TD([[makeQuery(id+"F19.imprint","IMPRINT",EDGE,{"derivedFrom":sQuery(id+"F19.wireOp",EDGE,"E65.4.1.0")}),1.0]])]});
            var Q15;
            Q15=makeQuery(id+"F19.imprint","IMPRINT",FACE,{"disambiguationData":[TD([[makeQuery(id+"F19.imprint","IMPRINT",EDGE,{"derivedFrom":sQuery(id+"F19.wireOp",EDGE,"E65.5.1.0")}),1.0]])]});
            var Q16;
            Q16=makeQuery(id+"F19.imprint","IMPRINT",FACE,{"disambiguationData":[TD([[makeQuery(id+"F19.imprint","IMPRINT",EDGE,{"derivedFrom":sQuery(id+"F19.wireOp",EDGE,"E65.6.1.0")}),1.0]])]});
            var Q17;
            Q17=makeQuery(id+"F19.imprint","IMPRINT",FACE,{"disambiguationData":[TD([[makeQuery(id+"F19.imprint","IMPRINT",EDGE,{"derivedFrom":sQuery(id+"F19.wireOp",EDGE,"E65.7.1.0")}),1.0]])]});
            var Q18;
            Q18=makeQuery(id+"F19.imprint","IMPRINT",FACE,{"disambiguationData":[TD([[makeQuery(id+"F19.imprint","IMPRINT",EDGE,{"derivedFrom":sQuery(id+"F19.wireOp",EDGE,"E65.8.1.0")}),1.0]])]});
            var Q19;
            Q19=makeQuery(id+"F19.imprint","IMPRINT",FACE,{"disambiguationData":[TD([[makeQuery(id+"F19.imprint","IMPRINT",EDGE,{"derivedFrom":sQuery(id+"F19.wireOp",EDGE,"E65.9.1.0")}),1.0]])]});
            extrude(context, id + "F20", {"entities" : qUnion([Q0, Q1, Q2, Q3, Q4, Q5, Q6, Q7, Q8, Q9, Q10, Q11, Q12, Q13, Q14, Q15, Q16, Q17, Q18, Q19]), "operationType" : NewBodyOperationType.REMOVE, "endBound" : BoundingType.THROUGH_ALL, "oppositeDirection" : true, "depth" : 25 * mm, "offsetDistance" : 25 * mm});
        }
        {
            var Q0;
            Q0=makeQuery(id+"F3.opExtrude","CAP_FACE",FACE,{"disambiguationData":[OSD([sQuery(id+"F2.wireOp",EDGE,"E42.bottom"),sQuery(id+"F2.wireOp",EDGE,"E42.top"),sQuery(id+"F2.wireOp",EDGE,"E42.left"),sQuery(id+"F2.wireOp",EDGE,"E44.0")])],"isStart":false});
            var sketch = newSketch(context, id + "F21", { "sketchPlane" : qUnion([Q0])});
            skCircle(sketch, "E66", {"center": v(58.56, 19.22) * mm, "radius": 7.5 * mm});
            skSolve(sketch);
        }
        {
            var Q0;
            Q0=makeQuery(id+"F21.imprint","IMPRINT",FACE,{"disambiguationData":[TD([[makeQuery(id+"F21.imprint","IMPRINT",EDGE,{"derivedFrom":sQuery(id+"F21.wireOp",EDGE,"E66")}),1.0]])]});
            extrude(context, id + "F22", {"entities" : qUnion([Q0]), "operationType" : NewBodyOperationType.REMOVE, "endBound" : BoundingType.THROUGH_ALL, "oppositeDirection" : true, "depth" : 25 * mm, "offsetDistance" : 25 * mm});
        }
    });
